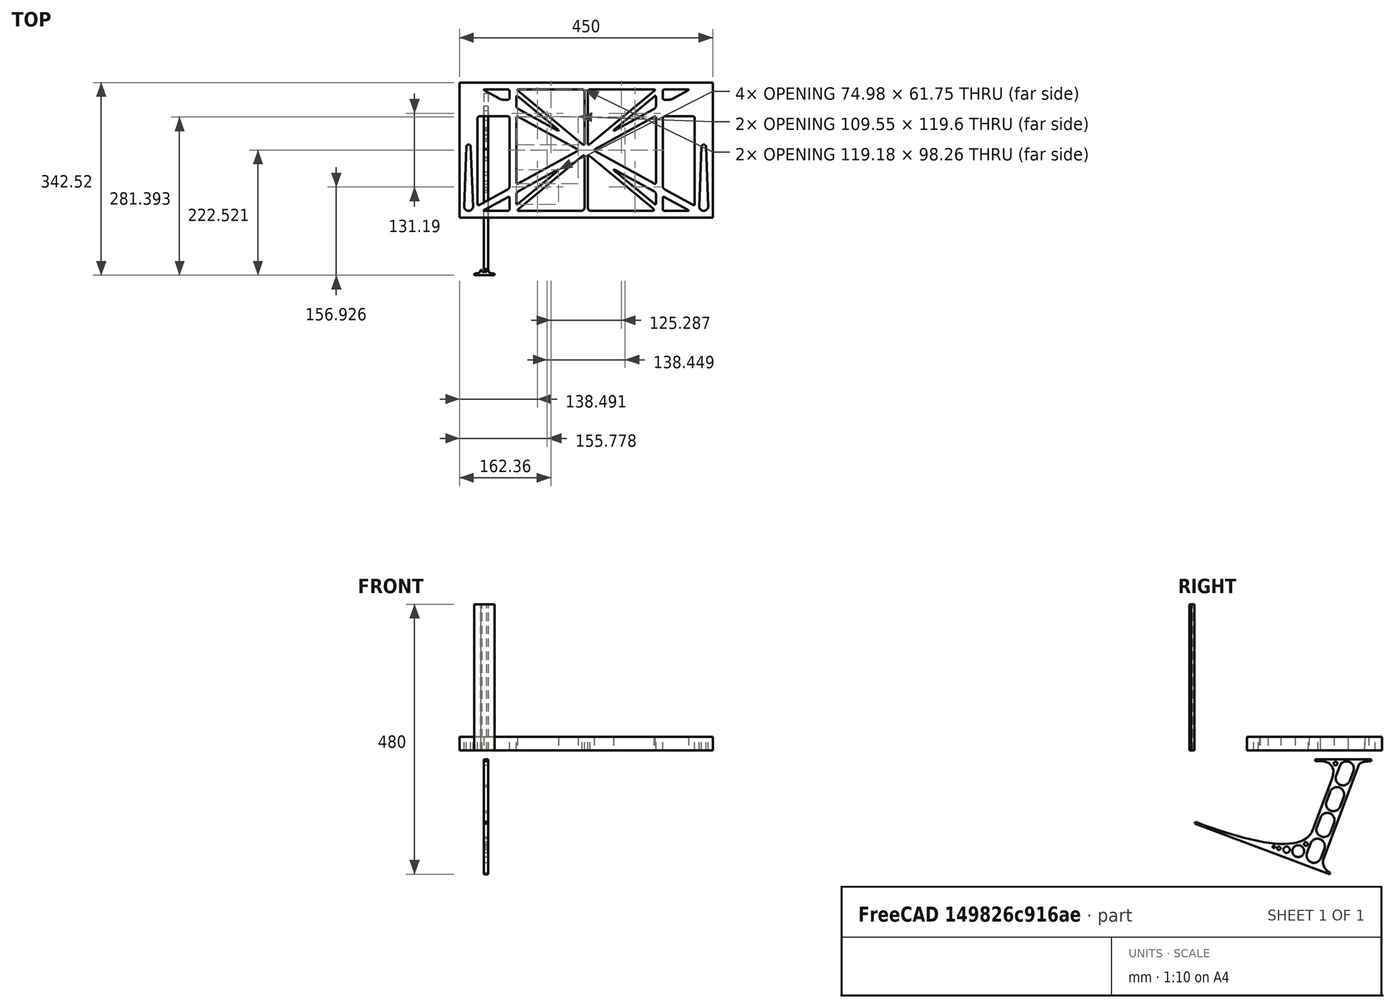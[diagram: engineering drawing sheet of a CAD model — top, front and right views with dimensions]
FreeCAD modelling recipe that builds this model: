
FCSTD DOCUMENT  (FreeCAD 0.19R0.19.2)
Label: laptopStand165FCStd
License: All rights reserved
LicenseURL: http://en.wikipedia.org/wiki/All_rights_reserved
objects: Sketcher::SketchObject×4, Part::Extrusion×3
note: 7 computed .brp shape members not serialized (recipe doc carries the construction recipe); baked Part::Feature solids carry a one-line shape summary decoded from their .brp

FEATURE [Sketcher::SketchObject] Sketch
  FullyConstrained = false
  sketch-geometry (349):
    g0: LineSegment StartX=-10.9272 StartY=-82.7794 StartZ=0 EndX=46.0728 EndY=-51.4823 EndZ=0
    g1: LineSegment StartX=-10.9272 StartY=76.4095 StartZ=0 EndX=-10.9272 EndY=-82.7794 EndZ=0
    g2: LineSegment StartX=46.0728 StartY=76.4095 StartZ=0 EndX=46.0728 EndY=-51.4823 EndZ=0
    g3: LineSegment StartX=-42.9272 StartY=136.221 StartZ=0 EndX=-42.9272 EndY=-103.779 EndZ=0
    g4: LineSegment StartX=407.073 StartY=136.221 StartZ=0 EndX=407.073 EndY=-103.779 EndZ=0
    g5: ArcOfCircle CenterX=-26.9272 CenterY=-83.7794 CenterZ=0 NormalX=0 NormalY=0 NormalZ=1 AngleXU=0 Radius=8 StartAngle=3.14159 EndAngle=6.28319
    g6: ArcOfCircle CenterX=391.073 CenterY=22.1087 CenterZ=0 NormalX=0 NormalY=0 NormalZ=1 AngleXU=0 Radius=8 StartAngle=-4.4e-15 EndAngle=3.14159
    g7: LineSegment StartX=399.073 StartY=22.1087 StartZ=0 EndX=399.073 EndY=-83.7794 EndZ=0
    g8: LineSegment StartX=383.073 StartY=22.1087 StartZ=0 EndX=383.073 EndY=-83.7794 EndZ=0
    g9: ArcOfCircle CenterX=391.073 CenterY=-83.7794 CenterZ=0 NormalX=0 NormalY=0 NormalZ=1 AngleXU=0 Radius=8 StartAngle=3.14159 EndAngle=6.28319
    g10: Circle CenterX=175.022 CenterY=27.0628 CenterZ=0 NormalX=0 NormalY=0 NormalZ=1 AngleXU=0 Radius=1
    g11: Circle CenterX=179.022 CenterY=24.8665 CenterZ=0 NormalX=0 NormalY=0 NormalZ=1 AngleXU=0 Radius=1
    g12: Circle CenterX=179.022 CenterY=27.0628 CenterZ=0 NormalX=0 NormalY=0 NormalZ=1 AngleXU=0 Radius=1
    g13: BSplineCurve PolesCount=3 KnotsCount=2 Degree=2 IsPeriodic=0
    g14: GeomPoint X=175.022 Y=27.0628 Z=0
    g15: GeomPoint X=179.022 Y=27.0628 Z=0
    g16: Circle CenterX=189.124 CenterY=27.0628 CenterZ=0 NormalX=0 NormalY=0 NormalZ=1 AngleXU=0 Radius=1
    g17: Circle CenterX=185.124 CenterY=24.8665 CenterZ=0 NormalX=0 NormalY=0 NormalZ=1 AngleXU=0 Radius=1
    g18: Circle CenterX=185.124 CenterY=27.0628 CenterZ=0 NormalX=0 NormalY=0 NormalZ=1 AngleXU=0 Radius=1
    g19: BSplineCurve PolesCount=3 KnotsCount=2 Degree=2 IsPeriodic=0
    g20: GeomPoint X=189.124 Y=27.0628 Z=0
    g21: GeomPoint X=185.124 Y=27.0628 Z=0
    g22: Circle CenterX=175.022 CenterY=5.37834 CenterZ=0 NormalX=0 NormalY=0 NormalZ=1 AngleXU=0 Radius=1
    g23: Circle CenterX=179.022 CenterY=7.57463 CenterZ=0 NormalX=0 NormalY=0 NormalZ=1 AngleXU=0 Radius=1
    g24: Circle CenterX=179.022 CenterY=5.34704 CenterZ=0 NormalX=0 NormalY=0 NormalZ=1 AngleXU=0 Radius=1
    g25: BSplineCurve PolesCount=3 KnotsCount=2 Degree=2 IsPeriodic=0
    g26: GeomPoint X=175.022 Y=5.37834 Z=0
    g27: GeomPoint X=179.022 Y=5.34704 Z=0
    g28: Circle CenterX=189.124 CenterY=5.37834 CenterZ=0 NormalX=0 NormalY=0 NormalZ=1 AngleXU=0 Radius=1
    g29: Circle CenterX=185.124 CenterY=7.57463 CenterZ=0 NormalX=0 NormalY=0 NormalZ=1 AngleXU=0 Radius=1
    g30: Circle CenterX=185.124 CenterY=5.34704 CenterZ=0 NormalX=0 NormalY=0 NormalZ=1 AngleXU=0 Radius=1
    g31: BSplineCurve PolesCount=3 KnotsCount=2 Degree=2 IsPeriodic=0
    g32: GeomPoint X=189.124 Y=5.37834 Z=0
    g33: GeomPoint X=185.124 Y=5.34704 Z=0
    g34: Circle CenterX=165.871 CenterY=18.1458 CenterZ=0 NormalX=0 NormalY=0 NormalZ=1 AngleXU=0 Radius=1
    g35: Circle CenterX=169.377 CenterY=16.2206 CenterZ=0 NormalX=0 NormalY=0 NormalZ=1 AngleXU=0 Radius=1
    g36: Circle CenterX=165.871 CenterY=14.2954 CenterZ=0 NormalX=0 NormalY=0 NormalZ=1 AngleXU=0 Radius=1
    g37: BSplineCurve PolesCount=3 KnotsCount=2 Degree=2 IsPeriodic=0
    g38: GeomPoint X=165.871 Y=18.1458 Z=0
    g39: GeomPoint X=165.871 Y=14.2954 Z=0
    g40: Circle CenterX=198.275 CenterY=18.1458 CenterZ=0 NormalX=0 NormalY=0 NormalZ=1 AngleXU=0 Radius=1
    g41: Circle CenterX=194.768 CenterY=16.2206 CenterZ=0 NormalX=0 NormalY=0 NormalZ=1 AngleXU=0 Radius=1
    g42: Circle CenterX=198.275 CenterY=14.2954 CenterZ=0 NormalX=0 NormalY=0 NormalZ=1 AngleXU=0 Radius=1
    g43: BSplineCurve PolesCount=3 KnotsCount=2 Degree=2 IsPeriodic=0
    g44: GeomPoint X=198.275 Y=18.1458 Z=0
    g45: GeomPoint X=198.275 Y=14.2954 Z=0
    g46: LineSegment StartX=407.073 StartY=-103.779 StartZ=0 EndX=-42.9272 EndY=-103.779 EndZ=0
    g47: LineSegment StartX=407.073 StartY=136.221 StartZ=0 EndX=-42.9272 EndY=136.221 EndZ=0
    g48: LineSegment StartX=46.0728 StartY=76.4095 StartZ=0 EndX=-10.9272 EndY=76.4095 EndZ=0
    g49: Circle CenterX=125.607 CenterY=54.1951 CenterZ=0 NormalX=0 NormalY=0 NormalZ=1 AngleXU=0 Radius=1
    g50: Circle CenterX=139.632 CenterY=46.4944 CenterZ=0 NormalX=0 NormalY=0 NormalZ=1 AngleXU=0 Radius=1
    g51: Circle CenterX=127.326 CenterY=56.7187 CenterZ=0 NormalX=0 NormalY=0 NormalZ=1 AngleXU=0 Radius=1
    g52: BSplineCurve PolesCount=3 KnotsCount=2 Degree=2 IsPeriodic=0
    g53: GeomPoint X=125.607 Y=54.1951 Z=0
    g54: GeomPoint X=127.326 Y=56.7187 Z=0
    g55: Circle CenterX=236.821 CenterY=56.7187 CenterZ=0 NormalX=0 NormalY=0 NormalZ=1 AngleXU=0 Radius=1
    g56: Circle CenterX=224.513 CenterY=46.4944 CenterZ=0 NormalX=0 NormalY=0 NormalZ=1 AngleXU=0 Radius=1
    g57: Circle CenterX=238.538 CenterY=54.1951 CenterZ=0 NormalX=0 NormalY=0 NormalZ=1 AngleXU=0 Radius=1
    g58: BSplineCurve PolesCount=3 KnotsCount=2 Degree=2 IsPeriodic=0
    g59: GeomPoint X=236.821 Y=56.7187 Z=0
    g60: GeomPoint X=238.538 Y=54.1951 Z=0
    g61: Circle CenterX=238.538 CenterY=-21.7539 CenterZ=0 NormalX=0 NormalY=0 NormalZ=1 AngleXU=0 Radius=1
    g62: Circle CenterX=224.513 CenterY=-14.0532 CenterZ=0 NormalX=0 NormalY=0 NormalZ=1 AngleXU=0 Radius=1
    g63: Circle CenterX=236.821 CenterY=-24.2775 CenterZ=0 NormalX=0 NormalY=0 NormalZ=1 AngleXU=0 Radius=1
    g64: BSplineCurve PolesCount=3 KnotsCount=2 Degree=2 IsPeriodic=0
    g65: GeomPoint X=238.538 Y=-21.7539 Z=0
    g66: GeomPoint X=236.821 Y=-24.2775 Z=0
    g67: Circle CenterX=125.607 CenterY=-21.7539 CenterZ=0 NormalX=0 NormalY=0 NormalZ=1 AngleXU=0 Radius=1
    g68: Circle CenterX=139.632 CenterY=-14.0532 CenterZ=0 NormalX=0 NormalY=0 NormalZ=1 AngleXU=0 Radius=1
    g69: Circle CenterX=127.325 CenterY=-24.2775 CenterZ=0 NormalX=0 NormalY=0 NormalZ=1 AngleXU=0 Radius=1
    g70: BSplineCurve PolesCount=3 KnotsCount=2 Degree=2 IsPeriodic=0
    g71: GeomPoint X=125.607 Y=-21.7539 Z=0
    g72: GeomPoint X=127.325 Y=-24.2775 Z=0
    g73: Circle CenterX=302.996 CenterY=111.695 CenterZ=0 NormalX=0 NormalY=0 NormalZ=1 AngleXU=0 Radius=1
    g74: Circle CenterX=306.073 CenterY=114.251 CenterZ=0 NormalX=0 NormalY=0 NormalZ=1 AngleXU=0 Radius=1
    g75: Circle CenterX=306.073 CenterY=110.251 CenterZ=0 NormalX=0 NormalY=0 NormalZ=1 AngleXU=0 Radius=1
    g76: BSplineCurve PolesCount=3 KnotsCount=2 Degree=2 IsPeriodic=0
    g77: GeomPoint X=302.996 Y=111.695 Z=0
    g78: GeomPoint X=306.073 Y=110.251 Z=0
    g79: Circle CenterX=306.073 CenterY=95.2763 CenterZ=0 NormalX=0 NormalY=0 NormalZ=1 AngleXU=0 Radius=1
    g80: Circle CenterX=306.073 CenterY=91.2763 CenterZ=0 NormalX=0 NormalY=0 NormalZ=1 AngleXU=0 Radius=1
    g81: Circle CenterX=302.567 CenterY=89.3511 CenterZ=0 NormalX=0 NormalY=0 NormalZ=1 AngleXU=0 Radius=1
    g82: BSplineCurve PolesCount=3 KnotsCount=2 Degree=2 IsPeriodic=0
    g83: GeomPoint X=306.073 Y=95.2763 Z=0
    g84: GeomPoint X=302.567 Y=89.3511 Z=0
    g85: LineSegment StartX=306.073 StartY=110.251 StartZ=0 EndX=306.073 EndY=95.2763 EndZ=0
    g86: LineSegment StartX=302.996 StartY=111.695 StartZ=0 EndX=236.821 EndY=56.7187 EndZ=0
    g87: LineSegment StartX=238.538 StartY=54.1951 StartZ=0 EndX=302.567 EndY=89.3511 EndZ=0
    g88: Circle CenterX=61.1496 CenterY=111.695 CenterZ=0 NormalX=0 NormalY=0 NormalZ=1 AngleXU=0 Radius=1
    g89: Circle CenterX=58.0728 CenterY=114.251 CenterZ=0 NormalX=0 NormalY=0 NormalZ=1 AngleXU=0 Radius=1
    g90: Circle CenterX=58.0728 CenterY=110.251 CenterZ=0 NormalX=0 NormalY=0 NormalZ=1 AngleXU=0 Radius=1
    g91: BSplineCurve PolesCount=3 KnotsCount=2 Degree=2 IsPeriodic=0
    g92: GeomPoint X=61.1496 Y=111.695 Z=0
    g93: GeomPoint X=58.0728 Y=110.251 Z=0
    g94: Circle CenterX=61.5791 CenterY=89.3511 CenterZ=0 NormalX=0 NormalY=0 NormalZ=1 AngleXU=0 Radius=1
    g95: Circle CenterX=58.0728 CenterY=91.2763 CenterZ=0 NormalX=0 NormalY=0 NormalZ=1 AngleXU=0 Radius=1
    g96: Circle CenterX=58.0728 CenterY=95.2763 CenterZ=0 NormalX=0 NormalY=0 NormalZ=1 AngleXU=0 Radius=1
    g97: BSplineCurve PolesCount=3 KnotsCount=2 Degree=2 IsPeriodic=0
    g98: GeomPoint X=61.5791 Y=89.3511 Z=0
    g99: GeomPoint X=58.0728 Y=95.2763 Z=0
    g100: LineSegment StartX=58.0728 StartY=110.251 StartZ=0 EndX=58.0728 EndY=95.2763 EndZ=0
    g101: LineSegment StartX=61.1496 StartY=111.695 StartZ=0 EndX=127.326 EndY=56.7187 EndZ=0
    g102: LineSegment StartX=125.607 StartY=54.1951 StartZ=0 EndX=61.5791 EndY=89.3511 EndZ=0
    g103: Circle CenterX=61.5791 CenterY=-56.9099 CenterZ=0 NormalX=0 NormalY=0 NormalZ=1 AngleXU=0 Radius=1
    g104: Circle CenterX=58.0728 CenterY=-58.8351 CenterZ=0 NormalX=0 NormalY=0 NormalZ=1 AngleXU=0 Radius=1
    g105: Circle CenterX=58.0728 CenterY=-62.8351 CenterZ=0 NormalX=0 NormalY=0 NormalZ=1 AngleXU=0 Radius=1
    g106: BSplineCurve PolesCount=3 KnotsCount=2 Degree=2 IsPeriodic=0
    g107: GeomPoint X=61.5791 Y=-56.9099 Z=0
    g108: GeomPoint X=58.0728 Y=-62.8351 Z=0
    g109: Circle CenterX=58.0728 CenterY=-77.8102 CenterZ=0 NormalX=0 NormalY=0 NormalZ=1 AngleXU=0 Radius=1
    g110: Circle CenterX=58.0728 CenterY=-81.8102 CenterZ=0 NormalX=0 NormalY=0 NormalZ=1 AngleXU=0 Radius=1
    g111: Circle CenterX=61.1496 CenterY=-79.2541 CenterZ=0 NormalX=0 NormalY=0 NormalZ=1 AngleXU=0 Radius=1
    g112: BSplineCurve PolesCount=3 KnotsCount=2 Degree=2 IsPeriodic=0
    g113: GeomPoint X=58.0728 Y=-77.8102 Z=0
    g114: GeomPoint X=61.1496 Y=-79.2541 Z=0
    g115: LineSegment StartX=58.0728 StartY=-62.8351 StartZ=0 EndX=58.0728 EndY=-77.8102 EndZ=0
    g116: LineSegment StartX=61.1496 StartY=-79.2541 StartZ=0 EndX=127.325 EndY=-24.2775 EndZ=0
    g117: LineSegment StartX=125.607 StartY=-21.7539 StartZ=0 EndX=61.5791 EndY=-56.9099 EndZ=0
    g118: Circle CenterX=302.567 CenterY=-56.9099 CenterZ=0 NormalX=0 NormalY=0 NormalZ=1 AngleXU=0 Radius=1
    g119: Circle CenterX=306.073 CenterY=-58.8351 CenterZ=0 NormalX=0 NormalY=0 NormalZ=1 AngleXU=0 Radius=1
    g120: Circle CenterX=306.073 CenterY=-62.8351 CenterZ=0 NormalX=0 NormalY=0 NormalZ=1 AngleXU=0 Radius=1
    g121: BSplineCurve PolesCount=3 KnotsCount=2 Degree=2 IsPeriodic=0
    g122: GeomPoint X=302.567 Y=-56.9099 Z=0
    g123: GeomPoint X=306.073 Y=-62.8351 Z=0
    g124: Circle CenterX=302.996 CenterY=-79.2541 CenterZ=0 NormalX=0 NormalY=0 NormalZ=1 AngleXU=0 Radius=1
    g125: Circle CenterX=306.073 CenterY=-81.8102 CenterZ=0 NormalX=0 NormalY=0 NormalZ=1 AngleXU=0 Radius=1
    g126: Circle CenterX=306.073 CenterY=-77.8102 CenterZ=0 NormalX=0 NormalY=0 NormalZ=1 AngleXU=0 Radius=1
    g127: BSplineCurve PolesCount=3 KnotsCount=2 Degree=2 IsPeriodic=0
    g128: GeomPoint X=302.996 Y=-79.2541 Z=0
    g129: GeomPoint X=306.073 Y=-77.8102 Z=0
    g130: LineSegment StartX=306.073 StartY=-62.8351 StartZ=0 EndX=306.073 EndY=-77.8102 EndZ=0
    g131: LineSegment StartX=302.996 StartY=-79.2541 StartZ=0 EndX=236.821 EndY=-24.2775 EndZ=0
    g132: LineSegment StartX=238.538 StartY=-21.7539 StartZ=0 EndX=302.567 EndY=-56.9099 EndZ=0
    g133: Circle CenterX=61.6457 CenterY=-88.8112 CenterZ=0 NormalX=0 NormalY=0 NormalZ=1 AngleXU=0 Radius=1
    g134: Circle CenterX=58.0728 CenterY=-91.7794 CenterZ=0 NormalX=0 NormalY=0 NormalZ=1 AngleXU=0 Radius=1
    g135: Circle CenterX=63.9135 CenterY=-91.7794 CenterZ=0 NormalX=0 NormalY=0 NormalZ=1 AngleXU=0 Radius=1
    g136: BSplineCurve PolesCount=3 KnotsCount=2 Degree=2 IsPeriodic=0
    g137: GeomPoint X=61.6457 Y=-88.8112 Z=0
    g138: GeomPoint X=63.9135 Y=-91.7794 Z=0
    g139: Circle CenterX=179.022 CenterY=-85.8163 CenterZ=0 NormalX=0 NormalY=0 NormalZ=1 AngleXU=0 Radius=1
    g140: Circle CenterX=179.022 CenterY=-91.7794 CenterZ=0 NormalX=0 NormalY=0 NormalZ=1 AngleXU=0 Radius=1
    g141: Circle CenterX=171.895 CenterY=-91.7794 CenterZ=0 NormalX=0 NormalY=0 NormalZ=1 AngleXU=0 Radius=1
    g142: BSplineCurve PolesCount=3 KnotsCount=2 Degree=2 IsPeriodic=0
    g143: GeomPoint X=179.022 Y=-85.8163 Z=0
    g144: GeomPoint X=171.895 Y=-91.7794 Z=0
    g145: Circle CenterX=185.124 CenterY=-86.2028 CenterZ=0 NormalX=0 NormalY=0 NormalZ=1 AngleXU=0 Radius=1
    g146: Circle CenterX=185.124 CenterY=-91.7794 CenterZ=0 NormalX=0 NormalY=0 NormalZ=1 AngleXU=0 Radius=1
    g147: Circle CenterX=191.747 CenterY=-91.7794 CenterZ=0 NormalX=0 NormalY=0 NormalZ=1 AngleXU=0 Radius=1
    g148: BSplineCurve PolesCount=3 KnotsCount=2 Degree=2 IsPeriodic=0
    g149: GeomPoint X=185.124 Y=-86.2028 Z=0
    g150: GeomPoint X=191.747 Y=-91.7794 Z=0
    g151: Circle CenterX=299.888 CenterY=-86.6413 CenterZ=0 NormalX=0 NormalY=0 NormalZ=1 AngleXU=0 Radius=1
    g152: Circle CenterX=306.073 CenterY=-91.7794 CenterZ=0 NormalX=0 NormalY=0 NormalZ=1 AngleXU=0 Radius=1
    g153: Circle CenterX=298.776 CenterY=-91.7794 CenterZ=0 NormalX=0 NormalY=0 NormalZ=1 AngleXU=0 Radius=1
    g154: BSplineCurve PolesCount=3 KnotsCount=2 Degree=2 IsPeriodic=0
    g155: GeomPoint X=299.888 Y=-86.6413 Z=0
    g156: GeomPoint X=298.776 Y=-91.7794 Z=0
    g157: LineSegment StartX=189.124 StartY=5.37834 StartZ=0 EndX=299.888 EndY=-86.6413 EndZ=0
    g158: LineSegment StartX=298.776 StartY=-91.7794 StartZ=0 EndX=191.747 EndY=-91.7794 EndZ=0
    g159: LineSegment StartX=185.124 StartY=-86.2028 StartZ=0 EndX=185.124 EndY=5.34704 EndZ=0
    g160: LineSegment StartX=179.022 StartY=5.34704 StartZ=0 EndX=179.022 EndY=-85.8163 EndZ=0
    g161: LineSegment StartX=171.895 StartY=-91.7794 StartZ=0 EndX=63.9135 EndY=-91.7794 EndZ=0
    g162: LineSegment StartX=61.6457 StartY=-88.8112 StartZ=0 EndX=175.022 EndY=5.37834 EndZ=0
    g163: Circle CenterX=302.073 CenterY=124.221 CenterZ=0 NormalX=0 NormalY=0 NormalZ=1 AngleXU=0 Radius=1
    g164: Circle CenterX=306.073 CenterY=124.221 CenterZ=0 NormalX=0 NormalY=0 NormalZ=1 AngleXU=0 Radius=1
    g165: Circle CenterX=302.996 CenterY=121.665 CenterZ=0 NormalX=0 NormalY=0 NormalZ=1 AngleXU=0 Radius=1
    g166: BSplineCurve PolesCount=3 KnotsCount=2 Degree=2 IsPeriodic=0
    g167: GeomPoint X=302.073 Y=124.221 Z=0
    g168: GeomPoint X=302.996 Y=121.665 Z=0
    g169: Circle CenterX=189.124 CenterY=124.221 CenterZ=0 NormalX=0 NormalY=0 NormalZ=1 AngleXU=0 Radius=1
    g170: Circle CenterX=185.124 CenterY=124.221 CenterZ=0 NormalX=0 NormalY=0 NormalZ=1 AngleXU=0 Radius=1
    g171: Circle CenterX=185.124 CenterY=120.221 CenterZ=0 NormalX=0 NormalY=0 NormalZ=1 AngleXU=0 Radius=1
    g172: BSplineCurve PolesCount=3 KnotsCount=2 Degree=2 IsPeriodic=0
    g173: GeomPoint X=189.124 Y=124.221 Z=0
    g174: GeomPoint X=185.124 Y=120.221 Z=0
    g175: Circle CenterX=175.022 CenterY=124.221 CenterZ=0 NormalX=0 NormalY=0 NormalZ=1 AngleXU=0 Radius=1
    g176: Circle CenterX=179.022 CenterY=124.221 CenterZ=0 NormalX=0 NormalY=0 NormalZ=1 AngleXU=0 Radius=1
    g177: Circle CenterX=179.022 CenterY=120.221 CenterZ=0 NormalX=0 NormalY=0 NormalZ=1 AngleXU=0 Radius=1
    g178: BSplineCurve PolesCount=3 KnotsCount=2 Degree=2 IsPeriodic=0
    g179: GeomPoint X=175.022 Y=124.221 Z=0
    g180: GeomPoint X=179.022 Y=120.221 Z=0
    g181: Circle CenterX=62.0728 CenterY=124.221 CenterZ=0 NormalX=0 NormalY=0 NormalZ=1 AngleXU=0 Radius=1
    g182: Circle CenterX=58.0728 CenterY=124.221 CenterZ=0 NormalX=0 NormalY=0 NormalZ=1 AngleXU=0 Radius=1
    g183: Circle CenterX=61.1496 CenterY=121.665 CenterZ=0 NormalX=0 NormalY=0 NormalZ=1 AngleXU=0 Radius=1
    g184: BSplineCurve PolesCount=3 KnotsCount=2 Degree=2 IsPeriodic=0
    g185: GeomPoint X=62.0728 Y=124.221 Z=0
    g186: GeomPoint X=61.1496 Y=121.665 Z=0
    g187: LineSegment StartX=62.0728 StartY=124.221 StartZ=0 EndX=175.022 EndY=124.221 EndZ=0
    g188: LineSegment StartX=179.022 StartY=120.221 StartZ=0 EndX=179.022 EndY=27.0628 EndZ=0
    g189: LineSegment StartX=185.124 StartY=27.0628 StartZ=0 EndX=185.124 EndY=120.221 EndZ=0
    g190: LineSegment StartX=189.124 StartY=124.221 StartZ=0 EndX=302.073 EndY=124.221 EndZ=0
    g191: LineSegment StartX=302.996 StartY=121.665 StartZ=0 EndX=189.124 EndY=27.0628 EndZ=0
    g192: LineSegment StartX=175.022 StartY=27.0628 StartZ=0 EndX=61.1496 EndY=121.665 EndZ=0
    g193: Circle CenterX=61.5791 CenterY=75.4095 CenterZ=0 NormalX=0 NormalY=0 NormalZ=1 AngleXU=0 Radius=1
    g194: Circle CenterX=58.0728 CenterY=77.3346 CenterZ=0 NormalX=0 NormalY=0 NormalZ=1 AngleXU=0 Radius=1
    g195: Circle CenterX=58.0728 CenterY=73.3346 CenterZ=0 NormalX=0 NormalY=0 NormalZ=1 AngleXU=0 Radius=1
    g196: BSplineCurve PolesCount=3 KnotsCount=2 Degree=2 IsPeriodic=0
    g197: GeomPoint X=61.5791 Y=75.4095 Z=0
    g198: GeomPoint X=58.0728 Y=73.3346 Z=0
    g199: Circle CenterX=58.0728 CenterY=-40.8935 CenterZ=0 NormalX=0 NormalY=0 NormalZ=1 AngleXU=0 Radius=1
    g200: Circle CenterX=58.0728 CenterY=-44.8935 CenterZ=0 NormalX=0 NormalY=0 NormalZ=1 AngleXU=0 Radius=1
    g201: Circle CenterX=61.5791 CenterY=-42.9683 CenterZ=0 NormalX=0 NormalY=0 NormalZ=1 AngleXU=0 Radius=1
    g202: BSplineCurve PolesCount=3 KnotsCount=2 Degree=2 IsPeriodic=0
    g203: GeomPoint X=58.0728 Y=-40.8935 Z=0
    g204: GeomPoint X=61.5791 Y=-42.9683 Z=0
    g205: LineSegment StartX=61.5791 StartY=-42.9683 StartZ=0 EndX=165.871 EndY=14.2954 EndZ=0
    g206: LineSegment StartX=165.871 StartY=18.1458 StartZ=0 EndX=61.5791 EndY=75.4095 EndZ=0
    g207: LineSegment StartX=58.0728 StartY=73.3346 StartZ=0 EndX=58.0728 EndY=-40.8935 EndZ=0
    g208: Circle CenterX=302.567 CenterY=-42.9683 CenterZ=0 NormalX=0 NormalY=0 NormalZ=1 AngleXU=0 Radius=1
    g209: Circle CenterX=306.073 CenterY=-44.8935 CenterZ=0 NormalX=0 NormalY=0 NormalZ=1 AngleXU=0 Radius=1
    g210: Circle CenterX=306.073 CenterY=-40.8935 CenterZ=0 NormalX=0 NormalY=0 NormalZ=1 AngleXU=0 Radius=1
    g211: BSplineCurve PolesCount=3 KnotsCount=2 Degree=2 IsPeriodic=0
    g212: GeomPoint X=302.567 Y=-42.9683 Z=0
    g213: GeomPoint X=306.073 Y=-40.8935 Z=0
    g214: Circle CenterX=306.073 CenterY=73.3346 CenterZ=0 NormalX=0 NormalY=0 NormalZ=1 AngleXU=0 Radius=1
    g215: Circle CenterX=306.073 CenterY=77.3346 CenterZ=0 NormalX=0 NormalY=0 NormalZ=1 AngleXU=0 Radius=1
    g216: Circle CenterX=302.567 CenterY=75.4095 CenterZ=0 NormalX=0 NormalY=0 NormalZ=1 AngleXU=0 Radius=1
    g217: BSplineCurve PolesCount=3 KnotsCount=2 Degree=2 IsPeriodic=0
    g218: GeomPoint X=306.073 Y=73.3346 Z=0
    g219: GeomPoint X=302.567 Y=75.4095 Z=0
    g220: LineSegment StartX=302.567 StartY=-42.9683 StartZ=0 EndX=198.275 EndY=14.2954 EndZ=0
    g221: LineSegment StartX=198.275 StartY=18.1458 StartZ=0 EndX=302.567 EndY=75.4095 EndZ=0
    g222: LineSegment StartX=306.073 StartY=73.3346 StartZ=0 EndX=306.073 EndY=-40.8935 EndZ=0
    g223: LineSegment StartX=322.073 StartY=105.865 StartZ=0 EndX=328.643 EndY=105.865 EndZ=0
    g224: LineSegment StartX=318.073 StartY=120.221 StartZ=0 EndX=318.073 EndY=109.865 EndZ=0
    g225: LineSegment StartX=336.157 StartY=107.779 StartZ=0 EndX=362.567 EndY=122.294 EndZ=0
    g226: Circle CenterX=362.073 CenterY=124.221 CenterZ=0 NormalX=0 NormalY=0 NormalZ=1 AngleXU=0 Radius=1
    g227: Circle CenterX=366.073 CenterY=124.221 CenterZ=0 NormalX=0 NormalY=0 NormalZ=1 AngleXU=0 Radius=1
    g228: Circle CenterX=362.567 CenterY=122.294 CenterZ=0 NormalX=0 NormalY=0 NormalZ=1 AngleXU=0 Radius=1
    g229: BSplineCurve PolesCount=3 KnotsCount=2 Degree=2 IsPeriodic=0
    g230: GeomPoint X=362.073 Y=124.221 Z=0
    g231: GeomPoint X=362.567 Y=122.294 Z=0
    g232: Circle CenterX=322.073 CenterY=124.221 CenterZ=0 NormalX=0 NormalY=0 NormalZ=1 AngleXU=0 Radius=1
    g233: Circle CenterX=318.073 CenterY=124.221 CenterZ=0 NormalX=0 NormalY=0 NormalZ=1 AngleXU=0 Radius=1
    g234: Circle CenterX=318.073 CenterY=120.221 CenterZ=0 NormalX=0 NormalY=0 NormalZ=1 AngleXU=0 Radius=1
    g235: BSplineCurve PolesCount=3 KnotsCount=2 Degree=2 IsPeriodic=0
    g236: GeomPoint X=322.073 Y=124.221 Z=0
    g237: GeomPoint X=318.073 Y=120.221 Z=0
    g238: Circle CenterX=322.073 CenterY=105.865 CenterZ=0 NormalX=0 NormalY=0 NormalZ=1 AngleXU=0 Radius=1
    g239: Circle CenterX=318.073 CenterY=105.865 CenterZ=0 NormalX=0 NormalY=0 NormalZ=1 AngleXU=0 Radius=1
    g240: Circle CenterX=318.073 CenterY=109.865 CenterZ=0 NormalX=0 NormalY=0 NormalZ=1 AngleXU=0 Radius=1
    g241: BSplineCurve PolesCount=3 KnotsCount=2 Degree=2 IsPeriodic=0
    g242: GeomPoint X=322.073 Y=105.865 Z=0
    g243: GeomPoint X=318.073 Y=109.865 Z=0
    g244: Circle CenterX=336.157 CenterY=107.779 CenterZ=0 NormalX=0 NormalY=0 NormalZ=1 AngleXU=0 Radius=1
    g245: Circle CenterX=332.651 CenterY=105.853 CenterZ=0 NormalX=0 NormalY=0 NormalZ=1 AngleXU=0 Radius=1
    g246: Circle CenterX=328.643 CenterY=105.865 CenterZ=0 NormalX=0 NormalY=0 NormalZ=1 AngleXU=0 Radius=1
    g247: BSplineCurve PolesCount=3 KnotsCount=2 Degree=2 IsPeriodic=0
    g248: GeomPoint X=336.157 Y=107.779 Z=0
    g249: GeomPoint X=328.643 Y=105.865 Z=0
    g250: LineSegment StartX=322.073 StartY=124.221 StartZ=0 EndX=362.073 EndY=124.221 EndZ=0
    g251: Circle CenterX=371.567 CenterY=-80.8644 CenterZ=0 NormalX=0 NormalY=0 NormalZ=1 AngleXU=0 Radius=1
    g252: Circle CenterX=375.073 CenterY=-82.7896 CenterZ=0 NormalX=0 NormalY=0 NormalZ=1 AngleXU=0 Radius=1
    g253: Circle CenterX=375.073 CenterY=-78.7896 CenterZ=0 NormalX=0 NormalY=0 NormalZ=1 AngleXU=0 Radius=1
    g254: BSplineCurve PolesCount=3 KnotsCount=2 Degree=2 IsPeriodic=0
    g255: GeomPoint X=371.567 Y=-80.8644 Z=0
    g256: GeomPoint X=375.073 Y=-78.7896 Z=0
    g257: Circle CenterX=321.579 CenterY=-53.4075 CenterZ=0 NormalX=0 NormalY=0 NormalZ=1 AngleXU=0 Radius=1
    g258: Circle CenterX=318.073 CenterY=-51.4823 CenterZ=0 NormalX=0 NormalY=0 NormalZ=1 AngleXU=0 Radius=1
    g259: Circle CenterX=318.073 CenterY=-47.4805 CenterZ=0 NormalX=0 NormalY=0 NormalZ=1 AngleXU=0 Radius=1
    g260: BSplineCurve PolesCount=3 KnotsCount=2 Degree=2 IsPeriodic=0
    g261: GeomPoint X=321.579 Y=-53.4075 Z=0
    g262: GeomPoint X=318.073 Y=-47.4805 Z=0
    g263: LineSegment StartX=371.567 StartY=-80.8644 StartZ=0 EndX=321.579 EndY=-53.4075 EndZ=0
    g264: Circle CenterX=321.579 CenterY=-67.3492 CenterZ=0 NormalX=0 NormalY=0 NormalZ=1 AngleXU=0 Radius=1
    g265: Circle CenterX=318.073 CenterY=-65.424 CenterZ=0 NormalX=0 NormalY=0 NormalZ=1 AngleXU=0 Radius=1
    g266: Circle CenterX=318.073 CenterY=-69.424 CenterZ=0 NormalX=0 NormalY=0 NormalZ=1 AngleXU=0 Radius=1
    g267: BSplineCurve PolesCount=3 KnotsCount=2 Degree=2 IsPeriodic=0
    g268: GeomPoint X=321.579 Y=-67.3492 Z=0
    g269: GeomPoint X=318.073 Y=-69.424 Z=0
    g270: Circle CenterX=362.567 CenterY=-89.8542 CenterZ=0 NormalX=0 NormalY=0 NormalZ=1 AngleXU=0 Radius=1
    g271: Circle CenterX=366.073 CenterY=-91.7794 CenterZ=0 NormalX=0 NormalY=0 NormalZ=1 AngleXU=0 Radius=1
    g272: Circle CenterX=362.073 CenterY=-91.7794 CenterZ=0 NormalX=0 NormalY=0 NormalZ=1 AngleXU=0 Radius=1
    g273: BSplineCurve PolesCount=3 KnotsCount=2 Degree=2 IsPeriodic=0
    g274: GeomPoint X=362.567 Y=-89.8542 Z=0
    g275: GeomPoint X=362.073 Y=-91.7794 Z=0
    g276: Circle CenterX=322.073 CenterY=-91.7794 CenterZ=0 NormalX=0 NormalY=0 NormalZ=1 AngleXU=0 Radius=1
    g277: Circle CenterX=318.073 CenterY=-91.7794 CenterZ=0 NormalX=0 NormalY=0 NormalZ=1 AngleXU=0 Radius=1
    g278: Circle CenterX=318.073 CenterY=-87.7794 CenterZ=0 NormalX=0 NormalY=0 NormalZ=1 AngleXU=0 Radius=1
    g279: BSplineCurve PolesCount=3 KnotsCount=2 Degree=2 IsPeriodic=0
    g280: GeomPoint X=322.073 Y=-91.7794 Z=0
    g281: GeomPoint X=318.073 Y=-87.7794 Z=0
    g282: LineSegment StartX=362.567 StartY=-89.8542 StartZ=0 EndX=321.579 EndY=-67.3492 EndZ=0
    g283: LineSegment StartX=318.073 StartY=-69.424 StartZ=0 EndX=318.073 EndY=-87.7794 EndZ=0
    g284: LineSegment StartX=322.073 StartY=-91.7794 StartZ=0 EndX=362.073 EndY=-91.7794 EndZ=0
    g285: Circle CenterX=2.07281 CenterY=124.221 CenterZ=0 NormalX=0 NormalY=0 NormalZ=1 AngleXU=0 Radius=1
    g286: Circle CenterX=1.57905 CenterY=122.295 CenterZ=0 NormalX=0 NormalY=0 NormalZ=1 AngleXU=0 Radius=1
    g287: BSplineCurve PolesCount=3 KnotsCount=2 Degree=2 IsPeriodic=0
    g288: GeomPoint X=2.07281 Y=124.221 Z=0
    g289: GeomPoint X=1.57905 Y=122.295 Z=0
    g290: Circle CenterX=42.0728 CenterY=124.221 CenterZ=0 NormalX=0 NormalY=0 NormalZ=1 AngleXU=0 Radius=1
    g291: Circle CenterX=46.0728 CenterY=124.221 CenterZ=0 NormalX=0 NormalY=0 NormalZ=1 AngleXU=0 Radius=1
    g292: Circle CenterX=46.0728 CenterY=120.221 CenterZ=0 NormalX=0 NormalY=0 NormalZ=1 AngleXU=0 Radius=1
    g293: BSplineCurve PolesCount=3 KnotsCount=2 Degree=2 IsPeriodic=0
    g294: GeomPoint X=42.0728 Y=124.221 Z=0
    g295: GeomPoint X=46.0728 Y=120.221 Z=0
    g296: Circle CenterX=46.0728 CenterY=109.865 CenterZ=0 NormalX=0 NormalY=0 NormalZ=1 AngleXU=0 Radius=1
    g297: Circle CenterX=46.0728 CenterY=105.865 CenterZ=0 NormalX=0 NormalY=0 NormalZ=1 AngleXU=0 Radius=1
    g298: Circle CenterX=42.0728 CenterY=105.865 CenterZ=0 NormalX=0 NormalY=0 NormalZ=1 AngleXU=0 Radius=1
    g299: BSplineCurve PolesCount=3 KnotsCount=2 Degree=2 IsPeriodic=0
    g300: GeomPoint X=46.0728 Y=109.865 Z=0
    g301: GeomPoint X=42.0728 Y=105.865 Z=0
    g302: Circle CenterX=35.5028 CenterY=105.865 CenterZ=0 NormalX=0 NormalY=0 NormalZ=1 AngleXU=0 Radius=1
    g303: Circle CenterX=31.5028 CenterY=105.865 CenterZ=0 NormalX=0 NormalY=0 NormalZ=1 AngleXU=0 Radius=1
    g304: Circle CenterX=27.9965 CenterY=107.79 CenterZ=0 NormalX=0 NormalY=0 NormalZ=1 AngleXU=0 Radius=1
    g305: BSplineCurve PolesCount=3 KnotsCount=2 Degree=2 IsPeriodic=0
    g306: GeomPoint X=35.5028 Y=105.865 Z=0
    g307: GeomPoint X=27.9965 Y=107.79 Z=0
    g308: LineSegment StartX=2.07281 StartY=124.221 StartZ=0 EndX=42.0728 EndY=124.221 EndZ=0
    g309: LineSegment StartX=46.0728 StartY=120.221 StartZ=0 EndX=46.0728 EndY=109.865 EndZ=0
    g310: LineSegment StartX=42.0728 StartY=105.865 StartZ=0 EndX=35.5028 EndY=105.865 EndZ=0
    g311: LineSegment StartX=27.9965 StartY=107.79 StartZ=0 EndX=1.57905 EndY=122.295 EndZ=0
    g312: Circle CenterX=42.5666 CenterY=-67.3492 CenterZ=0 NormalX=0 NormalY=0 NormalZ=1 AngleXU=0 Radius=1
    g313: Circle CenterX=46.0728 CenterY=-65.424 CenterZ=0 NormalX=0 NormalY=0 NormalZ=1 AngleXU=0 Radius=1
    g314: Circle CenterX=46.0728 CenterY=-69.424 CenterZ=0 NormalX=0 NormalY=0 NormalZ=1 AngleXU=0 Radius=1
    g315: BSplineCurve PolesCount=3 KnotsCount=2 Degree=2 IsPeriodic=0
    g316: GeomPoint X=42.5666 Y=-67.3492 Z=0
    g317: GeomPoint X=46.0728 Y=-69.424 Z=0
    g318: Circle CenterX=46.0728 CenterY=-87.7794 CenterZ=0 NormalX=0 NormalY=0 NormalZ=1 AngleXU=0 Radius=1
    g319: Circle CenterX=46.0728 CenterY=-91.7794 CenterZ=0 NormalX=0 NormalY=0 NormalZ=1 AngleXU=0 Radius=1
    g320: Circle CenterX=42.0728 CenterY=-91.7794 CenterZ=0 NormalX=0 NormalY=0 NormalZ=1 AngleXU=0 Radius=1
    g321: BSplineCurve PolesCount=3 KnotsCount=2 Degree=2 IsPeriodic=0
    g322: GeomPoint X=46.0728 Y=-87.7794 Z=0
    g323: GeomPoint X=42.0728 Y=-91.7794 Z=0
    g324: Circle CenterX=2.07281 CenterY=-91.7794 CenterZ=0 NormalX=0 NormalY=0 NormalZ=1 AngleXU=0 Radius=1
    g325: Circle CenterX=-1.92719 CenterY=-91.7794 CenterZ=0 NormalX=0 NormalY=0 NormalZ=1 AngleXU=0 Radius=1
    g326: Circle CenterX=1.57905 CenterY=-89.8542 CenterZ=0 NormalX=0 NormalY=0 NormalZ=1 AngleXU=0 Radius=1
    g327: BSplineCurve PolesCount=3 KnotsCount=2 Degree=2 IsPeriodic=0
    g328: GeomPoint X=2.07281 Y=-91.7794 Z=0
    g329: GeomPoint X=1.57905 Y=-89.8542 Z=0
    g330: LineSegment StartX=2.07281 StartY=-91.7794 StartZ=0 EndX=42.0728 EndY=-91.7794 EndZ=0
    g331: LineSegment StartX=46.0728 StartY=-87.7794 StartZ=0 EndX=46.0728 EndY=-69.424 EndZ=0
    g332: LineSegment StartX=42.5666 StartY=-67.3492 StartZ=0 EndX=1.57905 EndY=-89.8542 EndZ=0
    g333: Circle CenterX=322.073 CenterY=76.4095 CenterZ=0 NormalX=0 NormalY=0 NormalZ=1 AngleXU=0 Radius=4
    g334: BSplineCurve PolesCount=3 KnotsCount=2 Degree=2 IsPeriodic=0
    g335: GeomPoint X=318.073 Y=72.4095 Z=0
    g336: GeomPoint X=322.073 Y=76.4095 Z=0
    g337: Circle CenterX=375.073 CenterY=72.4095 CenterZ=0 NormalX=0 NormalY=0 NormalZ=1 AngleXU=0 Radius=1
    g338: Circle CenterX=375.073 CenterY=76.4095 CenterZ=0 NormalX=0 NormalY=0 NormalZ=1 AngleXU=0 Radius=1
    g339: Circle CenterX=371.073 CenterY=76.4095 CenterZ=0 NormalX=0 NormalY=0 NormalZ=1 AngleXU=0 Radius=1
    g340: BSplineCurve PolesCount=3 KnotsCount=2 Degree=2 IsPeriodic=0
    g341: GeomPoint X=375.073 Y=72.4095 Z=0
    g342: GeomPoint X=371.073 Y=76.4095 Z=0
    g343: LineSegment StartX=322.073 StartY=76.4095 StartZ=0 EndX=371.073 EndY=76.4095 EndZ=0
    g344: LineSegment StartX=318.073 StartY=72.4095 StartZ=0 EndX=318.073 EndY=-47.4805 EndZ=0
    g345: LineSegment StartX=375.073 StartY=72.4095 StartZ=0 EndX=375.073 EndY=-78.7896 EndZ=0
    g346: ArcOfCircle CenterX=-26.9272 CenterY=22.1087 CenterZ=0 NormalX=0 NormalY=0 NormalZ=1 AngleXU=0 Radius=4 StartAngle=5e-16 EndAngle=3.14159
    g347: LineSegment StartX=-30.9272 StartY=22.1087 StartZ=0 EndX=-34.9272 EndY=-83.7794 EndZ=0
    g348: LineSegment StartX=-18.9272 StartY=-83.7794 StartZ=0 EndX=-22.9272 EndY=22.1087 EndZ=0
  constraints (572):
    c: Coincident(g0,g2)
    c: Block(g0)
    c: Block(g1)
    c: Vertical(g3)
    c: Vertical(g4)
    c: Block(g4)
    c: Block(g3)
    c: Tangent(g6,g7) = 1.5708
    c: Tangent(g7,g9) = 1.5708
    c: Equal(g6,g9)
    c: Coincident(g8,g6)
    c: Coincident(g8,g9)
    c: Block(g7)
    c: Block(g8)
    c: Weight(g10) = 1
    c: Equal(g10,g11)
    c: Equal(g10,g12)
    c: InternalAlignment(g10,g13)
    c: InternalAlignment(g11,g13)
    c: InternalAlignment(g12,g13)
    c: InternalAlignment(g14,g13)
    c: InternalAlignment(g15,g13)
    c: Weight(g16) = 1
    c: Equal(g16,g17)
    c: Equal(g16,g18)
    c: InternalAlignment(g16,g19)
    c: InternalAlignment(g17,g19)
    c: InternalAlignment(g18,g19)
    c: InternalAlignment(g20,g19)
    c: InternalAlignment(g21,g19)
    c: Block(g19)
    c: Block(g13)
    c: Weight(g22) = 1
    c: Equal(g22,g23)
    c: Equal(g22,g24)
    c: InternalAlignment(g22,g25)
    c: InternalAlignment(g23,g25)
    c: InternalAlignment(g24,g25)
    c: InternalAlignment(g26,g25)
    c: InternalAlignment(g27,g25)
    c: Weight(g28) = 1
    c: Equal(g28,g29)
    c: Equal(g28,g30)
    c: InternalAlignment(g28,g31)
    c: InternalAlignment(g29,g31)
    c: InternalAlignment(g30,g31)
    c: InternalAlignment(g32,g31)
    c: InternalAlignment(g33,g31)
    c: Block(g31)
    c: Block(g25)
    c: Weight(g34) = 1
    c: Equal(g34,g35)
    c: Equal(g34,g36)
    c: InternalAlignment(g34,g37)
    c: InternalAlignment(g35,g37)
    c: InternalAlignment(g36,g37)
    c: InternalAlignment(g38,g37)
    c: InternalAlignment(g39,g37)
    c: Weight(g40) = 1
    c: Equal(g40,g41)
    c: Equal(g40,g42)
    c: InternalAlignment(g40,g43)
    c: InternalAlignment(g41,g43)
    c: InternalAlignment(g42,g43)
    c: InternalAlignment(g44,g43)
    c: InternalAlignment(g45,g43)
    c: Block(g37)
    c: Block(g43)
    c: Coincident(g46,g4)
    c: Coincident(g46,g3)
    c: Horizontal(g46)
    c: Distance(g46) = 450
    c: Coincident(g47,g4)
    c: Coincident(g47,g3)
    c: Horizontal(g47)
    c: Horizontal(g48)
    c: Coincident(g2,g48)
    c: Block(g48)
    c: Coincident(g1,g48)
    c: Weight(g49) = 1
    c: Equal(g49,g50)
    c: Equal(g49,g51)
    c: InternalAlignment(g49,g52)
    c: InternalAlignment(g50,g52)
    c: InternalAlignment(g51,g52)
    c: InternalAlignment(g53,g52)
    c: InternalAlignment(g54,g52)
    c: Block(g52)
    c: Weight(g55) = 1
    c: Equal(g55,g56)
    c: Equal(g55,g57)
    c: InternalAlignment(g55,g58)
    c: InternalAlignment(g56,g58)
    c: InternalAlignment(g57,g58)
    c: InternalAlignment(g59,g58)
    c: InternalAlignment(g60,g58)
    c: Block(g58)
    c: Weight(g61) = 1
    c: Equal(g61,g62)
    c: Equal(g61,g63)
    c: InternalAlignment(g61,g64)
    c: InternalAlignment(g62,g64)
    c: InternalAlignment(g63,g64)
    c: InternalAlignment(g65,g64)
    c: InternalAlignment(g66,g64)
    c: Block(g64)
    c: Weight(g67) = 1
    c: Equal(g67,g68)
    c: Equal(g67,g69)
    c: InternalAlignment(g67,g70)
    c: InternalAlignment(g68,g70)
    c: InternalAlignment(g69,g70)
    c: InternalAlignment(g71,g70)
    c: InternalAlignment(g72,g70)
    c: Block(g70)
    c: Weight(g73) = 1
    c: Equal(g73,g74)
    c: Equal(g73,g75)
    c: InternalAlignment(g73,g76)
    c: InternalAlignment(g74,g76)
    c: InternalAlignment(g75,g76)
    c: InternalAlignment(g77,g76)
    c: InternalAlignment(g78,g76)
    c: Weight(g79) = 1
    c: Equal(g79,g80)
    c: Equal(g79,g81)
    c: InternalAlignment(g79,g82)
    c: InternalAlignment(g80,g82)
    c: InternalAlignment(g81,g82)
    c: InternalAlignment(g83,g82)
    c: InternalAlignment(g84,g82)
    c: Block(g76)
    c: Block(g82)
    c: Coincident(g85,g76)
    c: Coincident(g85,g82)
    c: Vertical(g85)
    c: Coincident(g86,g76)
    c: Coincident(g86,g58)
    c: Coincident(g87,g58)
    c: Coincident(g87,g82)
    c: Weight(g88) = 1
    c: Equal(g88,g89)
    c: Equal(g88,g90)
    c: InternalAlignment(g88,g91)
    c: InternalAlignment(g89,g91)
    c: InternalAlignment(g90,g91)
    c: InternalAlignment(g92,g91)
    c: InternalAlignment(g93,g91)
    c: Weight(g94) = 1
    c: Equal(g94,g95)
    c: Equal(g94,g96)
    c: InternalAlignment(g94,g97)
    c: InternalAlignment(g95,g97)
    c: InternalAlignment(g96,g97)
    c: InternalAlignment(g98,g97)
    c: InternalAlignment(g99,g97)
    c: Block(g91)
    c: Block(g97)
    c: Coincident(g100,g91)
    c: Coincident(g100,g97)
    c: Vertical(g100)
    c: Coincident(g101,g91)
    c: Coincident(g101,g52)
    c: Coincident(g102,g52)
    c: Coincident(g102,g97)
    c: Weight(g103) = 1
    c: Equal(g103,g104)
    c: Equal(g103,g105)
    c: InternalAlignment(g103,g106)
    c: InternalAlignment(g104,g106)
    c: InternalAlignment(g105,g106)
    c: InternalAlignment(g107,g106)
    c: InternalAlignment(g108,g106)
    c: Weight(g109) = 1
    c: Equal(g109,g110)
    c: Equal(g109,g111)
    c: InternalAlignment(g109,g112)
    c: InternalAlignment(g110,g112)
    c: InternalAlignment(g111,g112)
    c: InternalAlignment(g113,g112)
    c: InternalAlignment(g114,g112)
    c: Block(g106)
    c: Block(g112)
    c: Coincident(g115,g106)
    c: Coincident(g115,g112)
    c: Vertical(g115)
    c: Coincident(g116,g112)
    c: Coincident(g116,g70)
    c: Coincident(g117,g70)
    c: Coincident(g117,g106)
    c: Weight(g118) = 1
    c: Equal(g118,g119)
    c: Equal(g118,g120)
    c: InternalAlignment(g118,g121)
    c: InternalAlignment(g119,g121)
    c: InternalAlignment(g120,g121)
    c: InternalAlignment(g122,g121)
    c: InternalAlignment(g123,g121)
    c: Weight(g124) = 1
    c: Equal(g124,g125)
    c: Equal(g124,g126)
    c: InternalAlignment(g124,g127)
    c: InternalAlignment(g125,g127)
    c: InternalAlignment(g126,g127)
    c: InternalAlignment(g128,g127)
    c: InternalAlignment(g129,g127)
    c: Block(g121)
    c: Block(g127)
    c: Coincident(g130,g121)
    c: Coincident(g130,g127)
    c: Vertical(g130)
    c: Coincident(g131,g127)
    c: Coincident(g131,g64)
    c: Coincident(g132,g64)
    c: Coincident(g132,g121)
    c: Weight(g133) = 1
    c: Equal(g133,g134)
    c: Equal(g133,g135)
    c: InternalAlignment(g133,g136)
    c: InternalAlignment(g134,g136)
    c: InternalAlignment(g135,g136)
    c: InternalAlignment(g137,g136)
    c: InternalAlignment(g138,g136)
    c: Weight(g139) = 1
    c: Equal(g139,g140)
    c: Equal(g139,g141)
    c: InternalAlignment(g139,g142)
    c: InternalAlignment(g140,g142)
    c: InternalAlignment(g141,g142)
    c: InternalAlignment(g143,g142)
    c: InternalAlignment(g144,g142)
    c: Weight(g145) = 1
    c: Equal(g145,g146)
    c: Equal(g145,g147)
    c: InternalAlignment(g145,g148)
    c: InternalAlignment(g146,g148)
    c: InternalAlignment(g147,g148)
    c: InternalAlignment(g149,g148)
    c: InternalAlignment(g150,g148)
    c: Weight(g151) = 1
    c: Equal(g151,g152)
    c: Equal(g151,g153)
    c: InternalAlignment(g151,g154)
    c: InternalAlignment(g152,g154)
    c: InternalAlignment(g153,g154)
    c: InternalAlignment(g155,g154)
    c: InternalAlignment(g156,g154)
    c: Block(g154)
    c: Block(g148)
    c: Block(g142)
    c: Block(g136)
    c: Coincident(g157,g31)
    c: Coincident(g157,g154)
    c: Coincident(g158,g154)
    c: Coincident(g158,g148)
    c: Horizontal(g158)
    c: Coincident(g159,g148)
    c: Coincident(g159,g31)
    c: Vertical(g159)
    c: Coincident(g160,g25)
    c: Coincident(g160,g142)
    c: Vertical(g160)
    c: Coincident(g161,g142)
    c: Coincident(g161,g136)
    c: Horizontal(g161)
    c: Coincident(g162,g136)
    c: Coincident(g162,g25)
    c: Weight(g163) = 1
    c: Equal(g163,g164)
    c: Equal(g163,g165)
    c: InternalAlignment(g163,g166)
    c: InternalAlignment(g164,g166)
    c: InternalAlignment(g165,g166)
    c: InternalAlignment(g167,g166)
    c: InternalAlignment(g168,g166)
    c: Weight(g169) = 1
    c: Equal(g169,g170)
    c: Equal(g169,g171)
    c: InternalAlignment(g169,g172)
    c: InternalAlignment(g170,g172)
    c: InternalAlignment(g171,g172)
    c: InternalAlignment(g173,g172)
    c: InternalAlignment(g174,g172)
    c: Weight(g175) = 1
    c: Equal(g175,g176)
    c: Equal(g175,g177)
    c: InternalAlignment(g175,g178)
    c: InternalAlignment(g176,g178)
    c: InternalAlignment(g177,g178)
    c: InternalAlignment(g179,g178)
    c: InternalAlignment(g180,g178)
    c: Weight(g181) = 1
    c: Equal(g181,g182)
    c: Equal(g181,g183)
    c: InternalAlignment(g181,g184)
    c: InternalAlignment(g182,g184)
    c: InternalAlignment(g183,g184)
    c: InternalAlignment(g185,g184)
    c: InternalAlignment(g186,g184)
    c: Block(g184)
    c: Block(g178)
    c: Block(g172)
    c: Block(g166)
    c: Coincident(g187,g184)
    c: Coincident(g187,g178)
    c: Horizontal(g187)
    c: Coincident(g188,g178)
    c: Coincident(g188,g13)
    c: Vertical(g188)
    c: Coincident(g189,g19)
    c: Coincident(g189,g172)
    c: Vertical(g189)
    c: Coincident(g190,g172)
    c: Coincident(g190,g166)
    c: Horizontal(g190)
    c: Coincident(g191,g166)
    c: Coincident(g191,g19)
    c: Coincident(g192,g13)
    c: Weight(g193) = 1
    c: Equal(g193,g194)
    c: Equal(g193,g195)
    c: InternalAlignment(g193,g196)
    c: InternalAlignment(g194,g196)
    c: InternalAlignment(g195,g196)
    c: InternalAlignment(g197,g196)
    c: InternalAlignment(g198,g196)
    c: Weight(g199) = 1
    c: Equal(g199,g200)
    c: Equal(g199,g201)
    c: InternalAlignment(g199,g202)
    c: InternalAlignment(g200,g202)
    c: InternalAlignment(g201,g202)
    c: InternalAlignment(g203,g202)
    c: InternalAlignment(g204,g202)
    c: Block(g202)
    c: Block(g196)
    c: Coincident(g205,g202)
    c: Coincident(g205,g37)
    c: Coincident(g206,g37)
    c: Coincident(g206,g196)
    c: Coincident(g207,g196)
    c: Coincident(g207,g202)
    c: Vertical(g207)
    c: Weight(g208) = 1
    c: Equal(g208,g209)
    c: Equal(g208,g210)
    c: InternalAlignment(g208,g211)
    c: InternalAlignment(g209,g211)
    c: InternalAlignment(g210,g211)
    c: InternalAlignment(g212,g211)
    c: InternalAlignment(g213,g211)
    c: Weight(g214) = 1
    c: Equal(g214,g215)
    c: Equal(g214,g216)
    c: InternalAlignment(g214,g217)
    c: InternalAlignment(g215,g217)
    c: InternalAlignment(g216,g217)
    c: InternalAlignment(g218,g217)
    c: InternalAlignment(g219,g217)
    c: Block(g217)
    c: Block(g211)
    c: Coincident(g220,g211)
    c: Coincident(g220,g43)
    c: Coincident(g221,g43)
    c: Coincident(g221,g217)
    c: Coincident(g222,g217)
    c: Coincident(g222,g211)
    c: Vertical(g222)
    c: Horizontal(g223)
    c: Block(g223)
    c: Vertical(g224)
    c: Block(g224)
    c: Block(g225)
    c: Weight(g226) = 1
    c: Equal(g226,g227)
    c: Equal(g226,g228)
    c: InternalAlignment(g226,g229)
    c: InternalAlignment(g227,g229)
    c: InternalAlignment(g228,g229)
    c: InternalAlignment(g230,g229)
    c: InternalAlignment(g231,g229)
    c: Weight(g232) = 1
    c: Equal(g232,g233)
    c: Equal(g232,g234)
    c: InternalAlignment(g232,g235)
    c: InternalAlignment(g233,g235)
    c: InternalAlignment(g234,g235)
    c: InternalAlignment(g236,g235)
    c: InternalAlignment(g237,g235)
    c: Weight(g238) = 1
    c: Equal(g238,g239)
    c: Equal(g238,g240)
    c: InternalAlignment(g238,g241)
    c: InternalAlignment(g239,g241)
    c: InternalAlignment(g240,g241)
    c: InternalAlignment(g242,g241)
    c: InternalAlignment(g243,g241)
    c: Weight(g244) = 1
    c: Equal(g244,g245)
    c: Equal(g244,g246)
    c: InternalAlignment(g244,g247)
    c: InternalAlignment(g245,g247)
    c: InternalAlignment(g246,g247)
    c: InternalAlignment(g248,g247)
    c: InternalAlignment(g249,g247)
    c: Block(g229)
    c: Block(g235)
    c: Block(g241)
    c: Block(g247)
    c: Coincident(g250,g235)
    c: Coincident(g250,g229)
    c: Horizontal(g250)
    c: Block(g192)
    c: Weight(g251) = 1
    c: Equal(g251,g252)
    c: Equal(g251,g253)
    c: InternalAlignment(g251,g254)
    c: InternalAlignment(g252,g254)
    c: InternalAlignment(g253,g254)
    c: InternalAlignment(g255,g254)
    c: InternalAlignment(g256,g254)
    c: Weight(g257) = 1
    c: Equal(g257,g258)
    c: Equal(g257,g259)
    c: InternalAlignment(g257,g260)
    c: InternalAlignment(g258,g260)
    c: InternalAlignment(g259,g260)
    c: InternalAlignment(g261,g260)
    c: InternalAlignment(g262,g260)
    c: Block(g254)
    c: Block(g260)
    c: Coincident(g263,g254)
    c: Coincident(g263,g260)
    c: Weight(g264) = 1
    c: Equal(g264,g265)
    c: Equal(g264,g266)
    c: InternalAlignment(g264,g267)
    c: InternalAlignment(g265,g267)
    c: InternalAlignment(g266,g267)
    c: InternalAlignment(g268,g267)
    c: InternalAlignment(g269,g267)
    c: Weight(g270) = 1
    c: Equal(g270,g271)
    c: Equal(g270,g272)
    c: InternalAlignment(g270,g273)
    c: InternalAlignment(g271,g273)
    c: InternalAlignment(g272,g273)
    c: InternalAlignment(g274,g273)
    c: InternalAlignment(g275,g273)
    c: Weight(g276) = 1
    c: Equal(g276,g277)
    c: Equal(g276,g278)
    c: InternalAlignment(g276,g279)
    c: InternalAlignment(g277,g279)
    c: InternalAlignment(g278,g279)
    c: InternalAlignment(g280,g279)
    c: InternalAlignment(g281,g279)
    c: Block(g279)
    c: Block(g273)
    c: Block(g267)
    c: Coincident(g282,g273)
    c: Coincident(g282,g267)
    c: Coincident(g283,g267)
    c: Coincident(g283,g279)
    c: Vertical(g283)
    c: Coincident(g284,g279)
    c: Coincident(g284,g273)
    c: Horizontal(g284)
    c: Weight(g285) = 1
    c: Equal(g285,g286)
    c: InternalAlignment(g285,g287)
    c: InternalAlignment(g286,g287)
    c: InternalAlignment(g288,g287)
    c: InternalAlignment(g289,g287)
    c: Weight(g290) = 1
    c: InternalAlignment(g291,g293)
    c: InternalAlignment(g292,g293)
    c: InternalAlignment(g294,g293)
    c: InternalAlignment(g295,g293)
    c: Weight(g296) = 1
    c: Equal(g296,g297)
    c: Equal(g296,g298)
    c: InternalAlignment(g296,g299)
    c: InternalAlignment(g297,g299)
    c: InternalAlignment(g298,g299)
    c: InternalAlignment(g300,g299)
    c: InternalAlignment(g301,g299)
    c: Equal(g302,g303)
    c: Equal(g302,g304)
    c: InternalAlignment(g302,g305)
    c: InternalAlignment(g303,g305)
    c: InternalAlignment(g304,g305)
    c: InternalAlignment(g306,g305)
    c: InternalAlignment(g307,g305)
    c: Block(g293)
    c: Block(g299)
    c: Block(g305)
    c: Block(g287)
    c: Coincident(g308,g287)
    c: Coincident(g308,g293)
    c: Horizontal(g308)
    c: Coincident(g309,g293)
    c: Coincident(g309,g299)
    c: Vertical(g309)
    c: Coincident(g310,g299)
    c: Coincident(g310,g305)
    c: Horizontal(g310)
    c: Coincident(g311,g305)
    c: Coincident(g311,g287)
    c: Weight(g312) = 1
    c: Equal(g312,g313)
    c: Equal(g312,g314)
    c: InternalAlignment(g312,g315)
    c: InternalAlignment(g313,g315)
    c: InternalAlignment(g314,g315)
    c: InternalAlignment(g316,g315)
    c: InternalAlignment(g317,g315)
    c: Weight(g318) = 1
    c: Equal(g318,g319)
    c: Equal(g318,g320)
    c: InternalAlignment(g318,g321)
    c: InternalAlignment(g319,g321)
    c: InternalAlignment(g320,g321)
    c: InternalAlignment(g322,g321)
    c: InternalAlignment(g323,g321)
    c: Weight(g324) = 1
    c: Equal(g324,g325)
    c: Equal(g324,g326)
    c: InternalAlignment(g324,g327)
    c: InternalAlignment(g325,g327)
    c: InternalAlignment(g326,g327)
    c: InternalAlignment(g328,g327)
    c: InternalAlignment(g329,g327)
    c: Block(g327)
    c: Block(g321)
    c: Block(g315)
    c: Coincident(g330,g327)
    c: Coincident(g330,g321)
    c: Horizontal(g330)
    c: Coincident(g331,g321)
    c: Coincident(g331,g315)
    c: Vertical(g331)
    c: Coincident(g332,g315)
    c: Coincident(g332,g327)
    c: InternalAlignment(g333,g334)
    c: InternalAlignment(g335,g334)
    c: InternalAlignment(g336,g334)
    c: Block(g334)
    c: Equal(g337,g338)
    c: Equal(g337,g339)
    c: InternalAlignment(g337,g340)
    c: InternalAlignment(g338,g340)
    c: InternalAlignment(g339,g340)
    c: InternalAlignment(g341,g340)
    c: InternalAlignment(g342,g340)
    c: Block(g340)
    c: Coincident(g343,g334)
    c: Horizontal(g343)
    c: Block(g343)
    c: Coincident(g344,g334)
    c: Coincident(g344,g260)
    c: Vertical(g344)
    c: Coincident(g345,g340)
    c: Coincident(g345,g254)
    c: Vertical(g345)
    c: Coincident(g347,g5)
    c: Coincident(g348,g5)
    c: Block(g346)
    c: Block(g5)
    c: Block(g348)
    c: Block(g347)
    c: Distance(g344) = 119.89
FEATURE [Sketcher::SketchObject] Sketch001
  FullyConstrained = true
  MapMode = 4
  Placement = pos=(0,0,0) rot=(0.57735,0.57735,0.57735;2.0944rad)
  Support = -> [Sketch]
  sketch-geometry (46):
    g0: BSplineCurve PolesCount=3 KnotsCount=2 Degree=2 IsPeriodic=0
    g1: ArcOfCircle CenterX=73.1223 CenterY=-32.291 CenterZ=0 NormalX=0 NormalY=0 NormalZ=1 AngleXU=0 Radius=13 StartAngle=5.92268 EndAngle=9.06428
    g2: ArcOfCircle CenterX=66.7816 CenterY=-49.1439 CenterZ=0 NormalX=0 NormalY=0 NormalZ=1 AngleXU=0 Radius=13 StartAngle=2.78068 EndAngle=5.92131
    g3: ArcOfCircle CenterX=55.9263 CenterY=-78.1807 CenterZ=0 NormalX=0 NormalY=0 NormalZ=1 AngleXU=0 Radius=13 StartAngle=5.92268 EndAngle=9.06428
    g4: ArcOfCircle CenterX=49.5884 CenterY=-95.0342 CenterZ=0 NormalX=0 NormalY=0 NormalZ=1 AngleXU=0 Radius=13 StartAngle=2.78068 EndAngle=5.92131
    g5: ArcOfCircle CenterX=38.7206 CenterY=-124.067 CenterZ=0 NormalX=0 NormalY=0 NormalZ=1 AngleXU=0 Radius=13 StartAngle=5.92268 EndAngle=9.06428
    g6: ArcOfCircle CenterX=32.3875 CenterY=-140.92 CenterZ=0 NormalX=0 NormalY=0 NormalZ=1 AngleXU=0 Radius=13 StartAngle=2.78068 EndAngle=5.92131
    g7: ArcOfCircle CenterX=21.4715 CenterY=-169.934 CenterZ=0 NormalX=0 NormalY=0 NormalZ=1 AngleXU=0 Radius=13 StartAngle=5.92268 EndAngle=9.06428
    g8: ArcOfCircle CenterX=15.1336 CenterY=-186.787 CenterZ=0 NormalX=0 NormalY=0 NormalZ=1 AngleXU=0 Radius=13 StartAngle=2.78068 EndAngle=5.92131
    g9-g12: Circle x4 (B-spline internal-alignment scaffolding for g13; pole/knot coordinates omitted)
    g13: BSplineCurve PolesCount=4 KnotsCount=2 Degree=3 IsPeriodic=0
    g14: GeomPoint X=28.8094 Y=-19.0875 Z=0
    g15: GeomPoint X=47.0443 Y=-50.4712 Z=0
    g16: Circle CenterX=53.5586 CenterY=-23.2695 CenterZ=0 NormalX=0 NormalY=0 NormalZ=1 AngleXU=0 Radius=3.24518
    g17: Circle CenterX=-195.441 CenterY=-127.082 CenterZ=0 NormalX=0 NormalY=0 NormalZ=1 AngleXU=0 Radius=1
    g18: Circle CenterX=-8.24091 CenterY=-197.481 CenterZ=0 NormalX=0 NormalY=0 NormalZ=1 AngleXU=0 Radius=1
    g19: Circle CenterX=12.8789 CenterY=-141.321 CenterZ=0 NormalX=0 NormalY=0 NormalZ=1 AngleXU=0 Radius=1
    g20: BSplineCurve PolesCount=3 KnotsCount=2 Degree=2 IsPeriodic=0
    g21: GeomPoint X=-195.441 Y=-127.082 Z=0
    g22: GeomPoint X=12.8789 Y=-141.321 Z=0
    g23: Circle CenterX=-12.8016 CenterY=-179.036 CenterZ=0 NormalX=0 NormalY=0 NormalZ=1 AngleXU=0 Radius=10.5072
    g24: Circle CenterX=0.933922 CenterY=-166.43 CenterZ=0 NormalX=0 NormalY=0 NormalZ=1 AngleXU=0 Radius=3.26661
    g25: Circle CenterX=-33.5518 CenterY=-176.44 CenterZ=0 NormalX=0 NormalY=0 NormalZ=1 AngleXU=0 Radius=5.64388
    g26: Circle CenterX=-47.2366 CenterY=-173.859 CenterZ=0 NormalX=0 NormalY=0 NormalZ=1 AngleXU=0 Radius=3.01653
    g27: Circle CenterX=-56.2595 CenterY=-171.456 CenterZ=0 NormalX=0 NormalY=0 NormalZ=1 AngleXU=0 Radius=2.12826
    g28: ArcOfCircle CenterX=51.2151 CenterY=-198.473 CenterZ=0 NormalX=0 NormalY=0 NormalZ=1 AngleXU=0 Radius=20 StartAngle=2.78189 EndAngle=4.35269
    g29: LineSegment StartX=32.4951 StartY=-191.433 StartZ=0 EndX=94.6578 EndY=-26.1352 EndZ=0
    g30: LineSegment StartX=43.1192 StartY=-220.001 StartZ=0 EndX=-196.497 EndY=-129.89 EndZ=0
    g31: LineSegment StartX=43.1192 StartY=-220.001 StartZ=0 EndX=44.1752 EndY=-217.193 EndZ=0
    g32: LineSegment StartX=117.223 StartY=-19.0875 StartZ=0 EndX=117.223 EndY=-16.0875 EndZ=0
    g33: LineSegment StartX=117.223 StartY=-16.0875 StartZ=0 EndX=17.2232 EndY=-16.0875 EndZ=0
    g34: LineSegment StartX=17.2232 StartY=-16.0875 StartZ=0 EndX=17.2232 EndY=-19.0875 EndZ=0
    g35: LineSegment StartX=28.8094 StartY=-19.0875 StartZ=0 EndX=17.2232 EndY=-19.0875 EndZ=0
    g36: LineSegment StartX=47.0443 StartY=-50.4712 StartZ=0 EndX=12.8789 EndY=-141.321 EndZ=0
    g37: LineSegment StartX=-195.441 StartY=-127.082 StartZ=0 EndX=-196.497 EndY=-129.89 EndZ=0
    g38: LineSegment StartX=85.2866 StartY=-36.8766 StartZ=0 EndX=78.9396 EndY=-53.7463 EndZ=0
    g39: LineSegment StartX=60.9579 StartY=-27.7053 StartZ=0 EndX=54.6191 EndY=-44.5532 EndZ=0
    g40: LineSegment StartX=68.0907 StartY=-82.7664 StartZ=0 EndX=61.7465 EndY=-99.6365 EndZ=0
    g41: LineSegment StartX=43.7619 StartY=-73.595 StartZ=0 EndX=37.426 EndY=-90.4435 EndZ=0
    g42: LineSegment StartX=50.885 StartY=-128.652 StartZ=0 EndX=44.5456 EndY=-145.522 EndZ=0
    g43: LineSegment StartX=26.5562 StartY=-119.481 StartZ=0 EndX=20.2251 EndY=-136.329 EndZ=0
    g44: LineSegment StartX=9.3071 StartY=-165.349 StartZ=0 EndX=2.97115 EndY=-182.197 EndZ=0
    g45: LineSegment StartX=33.6358 StartY=-174.52 StartZ=0 EndX=27.2917 EndY=-191.39 EndZ=0
  constraints (71):
    c: Block(g0)
    c: Block(g1)
    c: Block(g2)
    c: Block(g4)
    c: Block(g3)
    c: Block(g6)
    c: Block(g5)
    c: Block(g8)
    c: Block(g7)
    c: Weight(g9) = 1
    c: Equal(g9,g10)
    c: Equal(g9,g11)
    c: Equal(g9,g12)
    c: InternalAlignment(g9-g12 -> g13) x4
    c: InternalAlignment(g14,g13)
    c: InternalAlignment(g15,g13)
    c: Block(g16)
    c: Weight(g17) = 1
    c: Equal(g17,g18)
    c: Equal(g17,g19)
    c: InternalAlignment(g17,g20)
    c: InternalAlignment(g18,g20)
    c: InternalAlignment(g19,g20)
    c: InternalAlignment(g21,g20)
    c: InternalAlignment(g22,g20)
    c: Block(g20)
    c: Block(g23)
    c: Block(g24)
    c: Block(g25)
    c: Block(g26)
    c: Block(g27)
    c: Block(g28)
    c: Coincident(g29,g28)
    c: Coincident(g29,g0)
    c: Block(g13)
    c: Coincident(g31,g30)
    c: Coincident(g31,g28)
    c: Block(g31)
    c: Coincident(g32,g0)
    c: Vertical(g32)
    c: Coincident(g33,g32)
    c: Horizontal(g33)
    c: Coincident(g34,g33)
    c: Vertical(g34)
    c: Block(g33)
    c: Coincident(g35,g13)
    c: Coincident(g35,g34)
    c: Horizontal(g35)
    c: Coincident(g36,g13)
    c: Coincident(g36,g20)
    c: Coincident(g37,g20)
    c: Coincident(g37,g30)
    c: Block(g30)
    c: Coincident(g38,g1)
    c: Coincident(g38,g2)
    c: Coincident(g39,g1)
    c: Coincident(g39,g2)
    c: Coincident(g40,g3)
    c: Coincident(g40,g4)
    c: Coincident(g41,g3)
    c: Coincident(g41,g4)
    c: Coincident(g42,g5)
    c: Coincident(g42,g6)
    c: Coincident(g43,g5)
    c: Coincident(g43,g6)
    c: Coincident(g44,g7)
    c: Coincident(g44,g8)
    c: Coincident(g45,g7)
    c: Coincident(g45,g8)
    c: Distance(g30) = 256
    c: Distance(g33) = 100
FEATURE [Part::Extrusion] Extrude002
  Base = -> Sketch001
  Dir = (1,0,0)
  DirMode = 2
  FaceMakerClass = Part::FaceMakerBullseye
  LengthFwd = 8
  LengthRev = 0
  Solid = true
  Symmetric = false
FEATURE [Sketcher::SketchObject] Sketch002
  FullyConstrained = true
  sketch-geometry (20):
    g0: LineSegment StartX=-2.77179 StartY=-200.304 StartZ=0 EndX=5.22821 EndY=-200.304 EndZ=0
    g1: LineSegment StartX=5.22821 StartY=-200.304 StartZ=0 EndX=5.22821 EndY=-197.304 EndZ=0
    g2: LineSegment StartX=-2.77179 StartY=-200.304 StartZ=0 EndX=-2.77179 EndY=-197.304 EndZ=0
    g3: LineSegment StartX=5.22821 StartY=-197.304 StartZ=0 EndX=8.22821 EndY=-197.304 EndZ=0
    g4: LineSegment StartX=-2.77179 StartY=-197.304 StartZ=0 EndX=-5.77179 EndY=-197.304 EndZ=0
    g5: LineSegment StartX=19.2282 StartY=-203.304 StartZ=0 EndX=19.2282 EndY=-206.304 EndZ=0
    g6: LineSegment StartX=-16.7718 StartY=-203.304 StartZ=0 EndX=-16.7718 EndY=-206.304 EndZ=0
    g7: LineSegment StartX=-16.7718 StartY=-206.304 StartZ=0 EndX=19.2282 EndY=-206.304 EndZ=0
    g8: Circle CenterX=-16.7718 CenterY=-203.304 CenterZ=0 NormalX=0 NormalY=0 NormalZ=1 AngleXU=0 Radius=1
    g9: Circle CenterX=-5.77179 CenterY=-203.304 CenterZ=0 NormalX=0 NormalY=0 NormalZ=1 AngleXU=0 Radius=1
    g10: Circle CenterX=-5.77179 CenterY=-197.304 CenterZ=0 NormalX=0 NormalY=0 NormalZ=1 AngleXU=0 Radius=1
    g11: BSplineCurve PolesCount=3 KnotsCount=2 Degree=2 IsPeriodic=0
    g12: GeomPoint X=-16.7718 Y=-203.304 Z=0
    g13: GeomPoint X=-5.77179 Y=-197.304 Z=0
    g14: Circle CenterX=19.2282 CenterY=-203.304 CenterZ=0 NormalX=0 NormalY=0 NormalZ=1 AngleXU=0 Radius=1
    g15: Circle CenterX=8.22821 CenterY=-203.304 CenterZ=0 NormalX=0 NormalY=0 NormalZ=1 AngleXU=0 Radius=1
    g16: Circle CenterX=8.22821 CenterY=-197.304 CenterZ=0 NormalX=0 NormalY=0 NormalZ=1 AngleXU=0 Radius=1
    g17: BSplineCurve PolesCount=3 KnotsCount=2 Degree=2 IsPeriodic=0
    g18: GeomPoint X=19.2282 Y=-203.304 Z=0
    g19: GeomPoint X=8.22821 Y=-197.304 Z=0
  constraints (41):
    c: Horizontal(g0)
    c: Distance(g0) = 8
    c: Coincident(g1,g0)
    c: Vertical(g1)
    c: Distance(g1) = 3
    c: Coincident(g2,g0)
    c: Vertical(g2)
    c: Distance(g2) = 3
    c: Coincident(g3,g1)
    c: Horizontal(g3)
    c: Distance(g3) = 3
    c: Coincident(g4,g2)
    c: Horizontal(g4)
    c: Distance(g4) = 3
    c: Vertical(g5)
    c: Vertical(g6)
    c: Coincident(g7,g6)
    c: Coincident(g7,g5)
    c: Weight(g8) = 1
    c: Equal(g8,g9)
    c: Equal(g8,g10)
    c: Coincident(g11,g4)
    c: InternalAlignment(g8,g11)
    c: InternalAlignment(g9,g11)
    c: InternalAlignment(g10,g11)
    c: InternalAlignment(g12,g11)
    c: InternalAlignment(g13,g11)
    c: Coincident(g17,g5)
    c: Weight(g14) = 1
    c: Equal(g14,g15)
    c: Equal(g14,g16)
    c: Coincident(g17,g3)
    c: InternalAlignment(g14,g17)
    c: InternalAlignment(g15,g17)
    c: InternalAlignment(g16,g17)
    c: InternalAlignment(g18,g17)
    c: InternalAlignment(g19,g17)
    c: Block(g7)
    c: Block(g17)
    c: Block(g11)
    c: Block(g6)
FEATURE [Part::Extrusion] Extrude003
  Base = -> Sketch002
  Dir = (0,0,1)
  DirMode = 2
  FaceMakerClass = Part::FaceMakerBullseye
  LengthFwd = 260
  LengthRev = 0
  Solid = true
  Symmetric = false
FEATURE [Sketcher::SketchObject] Sketch003
  FullyConstrained = false
  sketch-geometry (398):
    g0: LineSegment StartX=-42.9272 StartY=136.221 StartZ=0 EndX=-42.9272 EndY=-103.779 EndZ=0
    g1: LineSegment StartX=407.073 StartY=136.221 StartZ=0 EndX=407.073 EndY=-103.779 EndZ=0
    g2: ArcOfCircle CenterX=-26.9272 CenterY=-83.7794 CenterZ=0 NormalX=0 NormalY=0 NormalZ=1 AngleXU=0 Radius=8 StartAngle=3.14159 EndAngle=6.28319
    g3: ArcOfCircle CenterX=391.073 CenterY=-83.7794 CenterZ=0 NormalX=0 NormalY=0 NormalZ=1 AngleXU=0 Radius=8 StartAngle=3.14159 EndAngle=6.28319
    g4: Circle CenterX=175.022 CenterY=27.0628 CenterZ=0 NormalX=0 NormalY=0 NormalZ=1 AngleXU=0 Radius=1
    g5: Circle CenterX=179.022 CenterY=24.8665 CenterZ=0 NormalX=0 NormalY=0 NormalZ=1 AngleXU=0 Radius=1
    g6: Circle CenterX=179.022 CenterY=27.0628 CenterZ=0 NormalX=0 NormalY=0 NormalZ=1 AngleXU=0 Radius=1
    g7: BSplineCurve PolesCount=3 KnotsCount=2 Degree=2 IsPeriodic=0
    g8: GeomPoint X=175.022 Y=27.0628 Z=0
    g9: GeomPoint X=179.022 Y=27.0628 Z=0
    g10: Circle CenterX=189.124 CenterY=27.0628 CenterZ=0 NormalX=0 NormalY=0 NormalZ=1 AngleXU=0 Radius=1
    g11: Circle CenterX=185.124 CenterY=24.8665 CenterZ=0 NormalX=0 NormalY=0 NormalZ=1 AngleXU=0 Radius=1
    g12: Circle CenterX=185.124 CenterY=27.0628 CenterZ=0 NormalX=0 NormalY=0 NormalZ=1 AngleXU=0 Radius=1
    g13: BSplineCurve PolesCount=3 KnotsCount=2 Degree=2 IsPeriodic=0
    g14: GeomPoint X=189.124 Y=27.0628 Z=0
    g15: GeomPoint X=185.124 Y=27.0628 Z=0
    g16: Circle CenterX=175.022 CenterY=5.37834 CenterZ=0 NormalX=0 NormalY=0 NormalZ=1 AngleXU=0 Radius=1
    g17: Circle CenterX=179.022 CenterY=7.57463 CenterZ=0 NormalX=0 NormalY=0 NormalZ=1 AngleXU=0 Radius=1
    g18: Circle CenterX=179.022 CenterY=5.34704 CenterZ=0 NormalX=0 NormalY=0 NormalZ=1 AngleXU=0 Radius=1
    g19: BSplineCurve PolesCount=3 KnotsCount=2 Degree=2 IsPeriodic=0
    g20: GeomPoint X=175.022 Y=5.37834 Z=0
    g21: GeomPoint X=179.022 Y=5.34704 Z=0
    g22: Circle CenterX=189.124 CenterY=5.37834 CenterZ=0 NormalX=0 NormalY=0 NormalZ=1 AngleXU=0 Radius=1
    g23: Circle CenterX=185.124 CenterY=7.57463 CenterZ=0 NormalX=0 NormalY=0 NormalZ=1 AngleXU=0 Radius=1
    g24: Circle CenterX=185.124 CenterY=5.34704 CenterZ=0 NormalX=0 NormalY=0 NormalZ=1 AngleXU=0 Radius=1
    g25: BSplineCurve PolesCount=3 KnotsCount=2 Degree=2 IsPeriodic=0
    g26: GeomPoint X=189.124 Y=5.37834 Z=0
    g27: GeomPoint X=185.124 Y=5.34704 Z=0
    g28: Circle CenterX=165.871 CenterY=18.1458 CenterZ=0 NormalX=0 NormalY=0 NormalZ=1 AngleXU=0 Radius=1
    g29: Circle CenterX=169.377 CenterY=16.2206 CenterZ=0 NormalX=0 NormalY=0 NormalZ=1 AngleXU=0 Radius=1
    g30: Circle CenterX=165.871 CenterY=14.2954 CenterZ=0 NormalX=0 NormalY=0 NormalZ=1 AngleXU=0 Radius=1
    g31: BSplineCurve PolesCount=3 KnotsCount=2 Degree=2 IsPeriodic=0
    g32: GeomPoint X=165.871 Y=18.1458 Z=0
    g33: GeomPoint X=165.871 Y=14.2954 Z=0
    g34: Circle CenterX=198.275 CenterY=18.1458 CenterZ=0 NormalX=0 NormalY=0 NormalZ=1 AngleXU=0 Radius=1
    g35: Circle CenterX=194.768 CenterY=16.2206 CenterZ=0 NormalX=0 NormalY=0 NormalZ=1 AngleXU=0 Radius=1
    g36: Circle CenterX=198.275 CenterY=14.2954 CenterZ=0 NormalX=0 NormalY=0 NormalZ=1 AngleXU=0 Radius=1
    g37: BSplineCurve PolesCount=3 KnotsCount=2 Degree=2 IsPeriodic=0
    g38: GeomPoint X=198.275 Y=18.1458 Z=0
    g39: GeomPoint X=198.275 Y=14.2954 Z=0
    g40: LineSegment StartX=407.073 StartY=-103.779 StartZ=0 EndX=-42.9272 EndY=-103.779 EndZ=0
    g41: Circle CenterX=125.607 CenterY=54.1951 CenterZ=0 NormalX=0 NormalY=0 NormalZ=1 AngleXU=0 Radius=1
    g42: Circle CenterX=139.632 CenterY=46.4944 CenterZ=0 NormalX=0 NormalY=0 NormalZ=1 AngleXU=0 Radius=1
    g43: Circle CenterX=127.326 CenterY=56.7187 CenterZ=0 NormalX=0 NormalY=0 NormalZ=1 AngleXU=0 Radius=1
    g44: BSplineCurve PolesCount=3 KnotsCount=2 Degree=2 IsPeriodic=0
    g45: GeomPoint X=125.607 Y=54.1951 Z=0
    g46: GeomPoint X=127.326 Y=56.7187 Z=0
    g47: Circle CenterX=236.821 CenterY=56.7187 CenterZ=0 NormalX=0 NormalY=0 NormalZ=1 AngleXU=0 Radius=1
    g48: Circle CenterX=224.513 CenterY=46.4944 CenterZ=0 NormalX=0 NormalY=0 NormalZ=1 AngleXU=0 Radius=1
    g49: Circle CenterX=238.538 CenterY=54.1951 CenterZ=0 NormalX=0 NormalY=0 NormalZ=1 AngleXU=0 Radius=1
    g50: BSplineCurve PolesCount=3 KnotsCount=2 Degree=2 IsPeriodic=0
    g51: GeomPoint X=236.821 Y=56.7187 Z=0
    g52: GeomPoint X=238.538 Y=54.1951 Z=0
    g53: Circle CenterX=238.538 CenterY=-21.7539 CenterZ=0 NormalX=0 NormalY=0 NormalZ=1 AngleXU=0 Radius=1
    g54: Circle CenterX=224.513 CenterY=-14.0532 CenterZ=0 NormalX=0 NormalY=0 NormalZ=1 AngleXU=0 Radius=1
    g55: Circle CenterX=236.821 CenterY=-24.2775 CenterZ=0 NormalX=0 NormalY=0 NormalZ=1 AngleXU=0 Radius=1
    g56: BSplineCurve PolesCount=3 KnotsCount=2 Degree=2 IsPeriodic=0
    g57: GeomPoint X=238.538 Y=-21.7539 Z=0
    g58: GeomPoint X=236.821 Y=-24.2775 Z=0
    g59: Circle CenterX=125.607 CenterY=-21.7539 CenterZ=0 NormalX=0 NormalY=0 NormalZ=1 AngleXU=0 Radius=1
    g60: Circle CenterX=139.632 CenterY=-14.0532 CenterZ=0 NormalX=0 NormalY=0 NormalZ=1 AngleXU=0 Radius=1
    g61: Circle CenterX=127.325 CenterY=-24.2775 CenterZ=0 NormalX=0 NormalY=0 NormalZ=1 AngleXU=0 Radius=1
    g62: BSplineCurve PolesCount=3 KnotsCount=2 Degree=2 IsPeriodic=0
    g63: GeomPoint X=125.607 Y=-21.7539 Z=0
    g64: GeomPoint X=127.325 Y=-24.2775 Z=0
    g65: Circle CenterX=302.996 CenterY=111.695 CenterZ=0 NormalX=0 NormalY=0 NormalZ=1 AngleXU=0 Radius=1
    g66: Circle CenterX=306.073 CenterY=114.251 CenterZ=0 NormalX=0 NormalY=0 NormalZ=1 AngleXU=0 Radius=1
    g67: Circle CenterX=306.073 CenterY=110.251 CenterZ=0 NormalX=0 NormalY=0 NormalZ=1 AngleXU=0 Radius=1
    g68: BSplineCurve PolesCount=3 KnotsCount=2 Degree=2 IsPeriodic=0
    g69: GeomPoint X=302.996 Y=111.695 Z=0
    g70: GeomPoint X=306.073 Y=110.251 Z=0
    g71: Circle CenterX=306.073 CenterY=95.2763 CenterZ=0 NormalX=0 NormalY=0 NormalZ=1 AngleXU=0 Radius=1
    g72: Circle CenterX=306.073 CenterY=91.2763 CenterZ=0 NormalX=0 NormalY=0 NormalZ=1 AngleXU=0 Radius=1
    g73: Circle CenterX=302.567 CenterY=89.3511 CenterZ=0 NormalX=0 NormalY=0 NormalZ=1 AngleXU=0 Radius=1
    g74: BSplineCurve PolesCount=3 KnotsCount=2 Degree=2 IsPeriodic=0
    g75: GeomPoint X=306.073 Y=95.2763 Z=0
    g76: GeomPoint X=302.567 Y=89.3511 Z=0
    g77: LineSegment StartX=306.073 StartY=110.251 StartZ=0 EndX=306.073 EndY=95.2763 EndZ=0
    g78: LineSegment StartX=302.996 StartY=111.695 StartZ=0 EndX=236.821 EndY=56.7187 EndZ=0
    g79: LineSegment StartX=238.538 StartY=54.1951 StartZ=0 EndX=302.567 EndY=89.3511 EndZ=0
    g80: Circle CenterX=61.1496 CenterY=111.695 CenterZ=0 NormalX=0 NormalY=0 NormalZ=1 AngleXU=0 Radius=1
    g81: Circle CenterX=58.0728 CenterY=114.251 CenterZ=0 NormalX=0 NormalY=0 NormalZ=1 AngleXU=0 Radius=1
    g82: Circle CenterX=58.0728 CenterY=110.251 CenterZ=0 NormalX=0 NormalY=0 NormalZ=1 AngleXU=0 Radius=1
    g83: BSplineCurve PolesCount=3 KnotsCount=2 Degree=2 IsPeriodic=0
    g84: GeomPoint X=61.1496 Y=111.695 Z=0
    g85: GeomPoint X=58.0728 Y=110.251 Z=0
    g86: Circle CenterX=61.5791 CenterY=89.3511 CenterZ=0 NormalX=0 NormalY=0 NormalZ=1 AngleXU=0 Radius=1
    g87: Circle CenterX=58.0728 CenterY=91.2763 CenterZ=0 NormalX=0 NormalY=0 NormalZ=1 AngleXU=0 Radius=1
    g88: Circle CenterX=58.0728 CenterY=95.2763 CenterZ=0 NormalX=0 NormalY=0 NormalZ=1 AngleXU=0 Radius=1
    g89: BSplineCurve PolesCount=3 KnotsCount=2 Degree=2 IsPeriodic=0
    g90: GeomPoint X=61.5791 Y=89.3511 Z=0
    g91: GeomPoint X=58.0728 Y=95.2763 Z=0
    g92: LineSegment StartX=58.0728 StartY=110.251 StartZ=0 EndX=58.0728 EndY=95.2763 EndZ=0
    g93: LineSegment StartX=61.1496 StartY=111.695 StartZ=0 EndX=127.326 EndY=56.7187 EndZ=0
    g94: LineSegment StartX=125.607 StartY=54.1951 StartZ=0 EndX=61.5791 EndY=89.3511 EndZ=0
    g95: Circle CenterX=61.5791 CenterY=-56.9099 CenterZ=0 NormalX=0 NormalY=0 NormalZ=1 AngleXU=0 Radius=1
    g96: Circle CenterX=58.0728 CenterY=-58.8351 CenterZ=0 NormalX=0 NormalY=0 NormalZ=1 AngleXU=0 Radius=1
    g97: Circle CenterX=58.0728 CenterY=-62.8351 CenterZ=0 NormalX=0 NormalY=0 NormalZ=1 AngleXU=0 Radius=1
    g98: BSplineCurve PolesCount=3 KnotsCount=2 Degree=2 IsPeriodic=0
    g99: GeomPoint X=61.5791 Y=-56.9099 Z=0
    g100: GeomPoint X=58.0728 Y=-62.8351 Z=0
    g101: Circle CenterX=58.0728 CenterY=-77.8102 CenterZ=0 NormalX=0 NormalY=0 NormalZ=1 AngleXU=0 Radius=1
    g102: Circle CenterX=58.0728 CenterY=-81.8102 CenterZ=0 NormalX=0 NormalY=0 NormalZ=1 AngleXU=0 Radius=1
    g103: Circle CenterX=61.1496 CenterY=-79.2541 CenterZ=0 NormalX=0 NormalY=0 NormalZ=1 AngleXU=0 Radius=1
    g104: BSplineCurve PolesCount=3 KnotsCount=2 Degree=2 IsPeriodic=0
    g105: GeomPoint X=58.0728 Y=-77.8102 Z=0
    g106: GeomPoint X=61.1496 Y=-79.2541 Z=0
    g107: LineSegment StartX=58.0728 StartY=-62.8351 StartZ=0 EndX=58.0728 EndY=-77.8102 EndZ=0
    g108: LineSegment StartX=61.1496 StartY=-79.2541 StartZ=0 EndX=127.325 EndY=-24.2775 EndZ=0
    g109: LineSegment StartX=125.607 StartY=-21.7539 StartZ=0 EndX=61.5791 EndY=-56.9099 EndZ=0
    g110: Circle CenterX=302.567 CenterY=-56.9099 CenterZ=0 NormalX=0 NormalY=0 NormalZ=1 AngleXU=0 Radius=1
    g111: Circle CenterX=306.073 CenterY=-58.8351 CenterZ=0 NormalX=0 NormalY=0 NormalZ=1 AngleXU=0 Radius=1
    g112: Circle CenterX=306.073 CenterY=-62.8351 CenterZ=0 NormalX=0 NormalY=0 NormalZ=1 AngleXU=0 Radius=1
    g113: BSplineCurve PolesCount=3 KnotsCount=2 Degree=2 IsPeriodic=0
    g114: GeomPoint X=302.567 Y=-56.9099 Z=0
    g115: GeomPoint X=306.073 Y=-62.8351 Z=0
    g116: Circle CenterX=302.996 CenterY=-79.2541 CenterZ=0 NormalX=0 NormalY=0 NormalZ=1 AngleXU=0 Radius=1
    g117: Circle CenterX=306.073 CenterY=-81.8102 CenterZ=0 NormalX=0 NormalY=0 NormalZ=1 AngleXU=0 Radius=1
    g118: Circle CenterX=306.073 CenterY=-77.8102 CenterZ=0 NormalX=0 NormalY=0 NormalZ=1 AngleXU=0 Radius=1
    g119: BSplineCurve PolesCount=3 KnotsCount=2 Degree=2 IsPeriodic=0
    g120: GeomPoint X=302.996 Y=-79.2541 Z=0
    g121: GeomPoint X=306.073 Y=-77.8102 Z=0
    g122: LineSegment StartX=306.073 StartY=-62.8351 StartZ=0 EndX=306.073 EndY=-77.8102 EndZ=0
    g123: LineSegment StartX=302.996 StartY=-79.2541 StartZ=0 EndX=236.821 EndY=-24.2775 EndZ=0
    g124: LineSegment StartX=238.538 StartY=-21.7539 StartZ=0 EndX=302.567 EndY=-56.9099 EndZ=0
    g125: Circle CenterX=61.6457 CenterY=-88.8112 CenterZ=0 NormalX=0 NormalY=0 NormalZ=1 AngleXU=0 Radius=1
    g126: Circle CenterX=58.0728 CenterY=-91.7794 CenterZ=0 NormalX=0 NormalY=0 NormalZ=1 AngleXU=0 Radius=1
    g127: Circle CenterX=63.9135 CenterY=-91.7794 CenterZ=0 NormalX=0 NormalY=0 NormalZ=1 AngleXU=0 Radius=1
    g128: BSplineCurve PolesCount=3 KnotsCount=2 Degree=2 IsPeriodic=0
    g129: GeomPoint X=61.6457 Y=-88.8112 Z=0
    g130: GeomPoint X=63.9135 Y=-91.7794 Z=0
    g131: Circle CenterX=179.022 CenterY=-85.8163 CenterZ=0 NormalX=0 NormalY=0 NormalZ=1 AngleXU=0 Radius=1
    g132: Circle CenterX=179.022 CenterY=-91.7794 CenterZ=0 NormalX=0 NormalY=0 NormalZ=1 AngleXU=0 Radius=1
    g133: Circle CenterX=171.895 CenterY=-91.7794 CenterZ=0 NormalX=0 NormalY=0 NormalZ=1 AngleXU=0 Radius=1
    g134: BSplineCurve PolesCount=3 KnotsCount=2 Degree=2 IsPeriodic=0
    g135: GeomPoint X=179.022 Y=-85.8163 Z=0
    g136: GeomPoint X=171.895 Y=-91.7794 Z=0
    g137: Circle CenterX=185.124 CenterY=-86.2028 CenterZ=0 NormalX=0 NormalY=0 NormalZ=1 AngleXU=0 Radius=1
    g138: Circle CenterX=185.124 CenterY=-91.7794 CenterZ=0 NormalX=0 NormalY=0 NormalZ=1 AngleXU=0 Radius=1
    g139: Circle CenterX=191.747 CenterY=-91.7794 CenterZ=0 NormalX=0 NormalY=0 NormalZ=1 AngleXU=0 Radius=1
    g140: BSplineCurve PolesCount=3 KnotsCount=2 Degree=2 IsPeriodic=0
    g141: GeomPoint X=185.124 Y=-86.2028 Z=0
    g142: GeomPoint X=191.747 Y=-91.7794 Z=0
    g143: Circle CenterX=299.888 CenterY=-86.6413 CenterZ=0 NormalX=0 NormalY=0 NormalZ=1 AngleXU=0 Radius=1
    g144: Circle CenterX=306.073 CenterY=-91.7794 CenterZ=0 NormalX=0 NormalY=0 NormalZ=1 AngleXU=0 Radius=1
    g145: Circle CenterX=298.776 CenterY=-91.7794 CenterZ=0 NormalX=0 NormalY=0 NormalZ=1 AngleXU=0 Radius=1
    g146: BSplineCurve PolesCount=3 KnotsCount=2 Degree=2 IsPeriodic=0
    g147: GeomPoint X=299.888 Y=-86.6413 Z=0
    g148: GeomPoint X=298.776 Y=-91.7794 Z=0
    g149: LineSegment StartX=189.124 StartY=5.37834 StartZ=0 EndX=299.888 EndY=-86.6413 EndZ=0
    g150: LineSegment StartX=298.776 StartY=-91.7794 StartZ=0 EndX=191.747 EndY=-91.7794 EndZ=0
    g151: LineSegment StartX=185.124 StartY=-86.2028 StartZ=0 EndX=185.124 EndY=5.34704 EndZ=0
    g152: LineSegment StartX=179.022 StartY=5.34704 StartZ=0 EndX=179.022 EndY=-85.8163 EndZ=0
    g153: LineSegment StartX=171.895 StartY=-91.7794 StartZ=0 EndX=63.9135 EndY=-91.7794 EndZ=0
    g154: LineSegment StartX=61.6457 StartY=-88.8112 StartZ=0 EndX=175.022 EndY=5.37834 EndZ=0
    g155: Circle CenterX=302.073 CenterY=124.221 CenterZ=0 NormalX=0 NormalY=0 NormalZ=1 AngleXU=0 Radius=1
    g156: Circle CenterX=306.073 CenterY=124.221 CenterZ=0 NormalX=0 NormalY=0 NormalZ=1 AngleXU=0 Radius=1
    g157: Circle CenterX=302.996 CenterY=121.665 CenterZ=0 NormalX=0 NormalY=0 NormalZ=1 AngleXU=0 Radius=1
    g158: BSplineCurve PolesCount=3 KnotsCount=2 Degree=2 IsPeriodic=0
    g159: GeomPoint X=302.073 Y=124.221 Z=0
    g160: GeomPoint X=302.996 Y=121.665 Z=0
    g161: Circle CenterX=189.124 CenterY=124.221 CenterZ=0 NormalX=0 NormalY=0 NormalZ=1 AngleXU=0 Radius=1
    g162: Circle CenterX=185.124 CenterY=124.221 CenterZ=0 NormalX=0 NormalY=0 NormalZ=1 AngleXU=0 Radius=1
    g163: Circle CenterX=185.124 CenterY=120.221 CenterZ=0 NormalX=0 NormalY=0 NormalZ=1 AngleXU=0 Radius=1
    g164: BSplineCurve PolesCount=3 KnotsCount=2 Degree=2 IsPeriodic=0
    g165: GeomPoint X=189.124 Y=124.221 Z=0
    g166: GeomPoint X=185.124 Y=120.221 Z=0
    g167: Circle CenterX=175.022 CenterY=124.221 CenterZ=0 NormalX=0 NormalY=0 NormalZ=1 AngleXU=0 Radius=1
    g168: Circle CenterX=179.022 CenterY=124.221 CenterZ=0 NormalX=0 NormalY=0 NormalZ=1 AngleXU=0 Radius=1
    g169: Circle CenterX=179.022 CenterY=120.221 CenterZ=0 NormalX=0 NormalY=0 NormalZ=1 AngleXU=0 Radius=1
    g170: BSplineCurve PolesCount=3 KnotsCount=2 Degree=2 IsPeriodic=0
    g171: GeomPoint X=175.022 Y=124.221 Z=0
    g172: GeomPoint X=179.022 Y=120.221 Z=0
    g173: Circle CenterX=62.0728 CenterY=124.221 CenterZ=0 NormalX=0 NormalY=0 NormalZ=1 AngleXU=0 Radius=1
    g174: Circle CenterX=58.0728 CenterY=124.221 CenterZ=0 NormalX=0 NormalY=0 NormalZ=1 AngleXU=0 Radius=1
    g175: Circle CenterX=61.1496 CenterY=121.665 CenterZ=0 NormalX=0 NormalY=0 NormalZ=1 AngleXU=0 Radius=1
    g176: BSplineCurve PolesCount=3 KnotsCount=2 Degree=2 IsPeriodic=0
    g177: GeomPoint X=62.0728 Y=124.221 Z=0
    g178: GeomPoint X=61.1496 Y=121.665 Z=0
    g179: LineSegment StartX=179.022 StartY=120.221 StartZ=0 EndX=179.022 EndY=27.0628 EndZ=0
    g180: LineSegment StartX=185.124 StartY=27.0628 StartZ=0 EndX=185.124 EndY=120.221 EndZ=0
    g181: LineSegment StartX=302.996 StartY=121.665 StartZ=0 EndX=189.124 EndY=27.0628 EndZ=0
    g182: LineSegment StartX=175.022 StartY=27.0628 StartZ=0 EndX=61.1496 EndY=121.665 EndZ=0
    g183: Circle CenterX=61.5791 CenterY=75.4095 CenterZ=0 NormalX=0 NormalY=0 NormalZ=1 AngleXU=0 Radius=1
    g184: Circle CenterX=58.0728 CenterY=77.3346 CenterZ=0 NormalX=0 NormalY=0 NormalZ=1 AngleXU=0 Radius=1
    g185: Circle CenterX=58.0728 CenterY=73.3346 CenterZ=0 NormalX=0 NormalY=0 NormalZ=1 AngleXU=0 Radius=1
    g186: BSplineCurve PolesCount=3 KnotsCount=2 Degree=2 IsPeriodic=0
    g187: GeomPoint X=61.5791 Y=75.4095 Z=0
    g188: GeomPoint X=58.0728 Y=73.3346 Z=0
    g189: Circle CenterX=58.0728 CenterY=-40.8935 CenterZ=0 NormalX=0 NormalY=0 NormalZ=1 AngleXU=0 Radius=1
    g190: Circle CenterX=58.0728 CenterY=-44.8935 CenterZ=0 NormalX=0 NormalY=0 NormalZ=1 AngleXU=0 Radius=1
    g191: Circle CenterX=61.5791 CenterY=-42.9683 CenterZ=0 NormalX=0 NormalY=0 NormalZ=1 AngleXU=0 Radius=1
    g192: BSplineCurve PolesCount=3 KnotsCount=2 Degree=2 IsPeriodic=0
    g193: GeomPoint X=58.0728 Y=-40.8935 Z=0
    g194: GeomPoint X=61.5791 Y=-42.9683 Z=0
    g195: LineSegment StartX=61.5791 StartY=-42.9683 StartZ=0 EndX=165.871 EndY=14.2954 EndZ=0
    g196: LineSegment StartX=165.871 StartY=18.1458 StartZ=0 EndX=61.5791 EndY=75.4095 EndZ=0
    g197: LineSegment StartX=58.0728 StartY=73.3346 StartZ=0 EndX=58.0728 EndY=-40.8935 EndZ=0
    g198: Circle CenterX=302.567 CenterY=-42.9683 CenterZ=0 NormalX=0 NormalY=0 NormalZ=1 AngleXU=0 Radius=1
    g199: Circle CenterX=306.073 CenterY=-44.8935 CenterZ=0 NormalX=0 NormalY=0 NormalZ=1 AngleXU=0 Radius=1
    g200: Circle CenterX=306.073 CenterY=-40.8935 CenterZ=0 NormalX=0 NormalY=0 NormalZ=1 AngleXU=0 Radius=1
    g201: BSplineCurve PolesCount=3 KnotsCount=2 Degree=2 IsPeriodic=0
    g202: GeomPoint X=302.567 Y=-42.9683 Z=0
    g203: GeomPoint X=306.073 Y=-40.8935 Z=0
    g204: Circle CenterX=306.073 CenterY=73.3346 CenterZ=0 NormalX=0 NormalY=0 NormalZ=1 AngleXU=0 Radius=1
    g205: Circle CenterX=306.073 CenterY=77.3346 CenterZ=0 NormalX=0 NormalY=0 NormalZ=1 AngleXU=0 Radius=1
    g206: Circle CenterX=302.567 CenterY=75.4095 CenterZ=0 NormalX=0 NormalY=0 NormalZ=1 AngleXU=0 Radius=1
    g207: BSplineCurve PolesCount=3 KnotsCount=2 Degree=2 IsPeriodic=0
    g208: GeomPoint X=306.073 Y=73.3346 Z=0
    g209: GeomPoint X=302.567 Y=75.4095 Z=0
    g210: LineSegment StartX=302.567 StartY=-42.9683 StartZ=0 EndX=198.275 EndY=14.2954 EndZ=0
    g211: LineSegment StartX=198.275 StartY=18.1458 StartZ=0 EndX=302.567 EndY=75.4095 EndZ=0
    g212: LineSegment StartX=306.073 StartY=73.3346 StartZ=0 EndX=306.073 EndY=-40.8935 EndZ=0
    g213: LineSegment StartX=322.073 StartY=105.865 StartZ=0 EndX=328.643 EndY=105.865 EndZ=0
    g214: LineSegment StartX=318.073 StartY=120.221 StartZ=0 EndX=318.073 EndY=109.865 EndZ=0
    g215: LineSegment StartX=336.157 StartY=107.779 StartZ=0 EndX=362.567 EndY=122.294 EndZ=0
    g216: Circle CenterX=362.073 CenterY=124.221 CenterZ=0 NormalX=0 NormalY=0 NormalZ=1 AngleXU=0 Radius=1
    g217: Circle CenterX=366.073 CenterY=124.221 CenterZ=0 NormalX=0 NormalY=0 NormalZ=1 AngleXU=0 Radius=1
    g218: Circle CenterX=362.567 CenterY=122.294 CenterZ=0 NormalX=0 NormalY=0 NormalZ=1 AngleXU=0 Radius=1
    g219: BSplineCurve PolesCount=3 KnotsCount=2 Degree=2 IsPeriodic=0
    g220: GeomPoint X=362.073 Y=124.221 Z=0
    g221: GeomPoint X=362.567 Y=122.294 Z=0
    g222: Circle CenterX=322.073 CenterY=124.221 CenterZ=0 NormalX=0 NormalY=0 NormalZ=1 AngleXU=0 Radius=1
    g223: Circle CenterX=318.073 CenterY=124.221 CenterZ=0 NormalX=0 NormalY=0 NormalZ=1 AngleXU=0 Radius=1
    g224: Circle CenterX=318.073 CenterY=120.221 CenterZ=0 NormalX=0 NormalY=0 NormalZ=1 AngleXU=0 Radius=1
    g225: BSplineCurve PolesCount=3 KnotsCount=2 Degree=2 IsPeriodic=0
    g226: GeomPoint X=322.073 Y=124.221 Z=0
    g227: GeomPoint X=318.073 Y=120.221 Z=0
    g228: Circle CenterX=322.073 CenterY=105.865 CenterZ=0 NormalX=0 NormalY=0 NormalZ=1 AngleXU=0 Radius=1
    g229: Circle CenterX=318.073 CenterY=105.865 CenterZ=0 NormalX=0 NormalY=0 NormalZ=1 AngleXU=0 Radius=1
    g230: Circle CenterX=318.073 CenterY=109.865 CenterZ=0 NormalX=0 NormalY=0 NormalZ=1 AngleXU=0 Radius=1
    g231: BSplineCurve PolesCount=3 KnotsCount=2 Degree=2 IsPeriodic=0
    g232: GeomPoint X=322.073 Y=105.865 Z=0
    g233: GeomPoint X=318.073 Y=109.865 Z=0
    g234: Circle CenterX=336.157 CenterY=107.779 CenterZ=0 NormalX=0 NormalY=0 NormalZ=1 AngleXU=0 Radius=1
    g235: Circle CenterX=332.651 CenterY=105.853 CenterZ=0 NormalX=0 NormalY=0 NormalZ=1 AngleXU=0 Radius=1
    g236: Circle CenterX=328.643 CenterY=105.865 CenterZ=0 NormalX=0 NormalY=0 NormalZ=1 AngleXU=0 Radius=1
    g237: BSplineCurve PolesCount=3 KnotsCount=2 Degree=2 IsPeriodic=0
    g238: GeomPoint X=336.157 Y=107.779 Z=0
    g239: GeomPoint X=328.643 Y=105.865 Z=0
    g240: LineSegment StartX=322.073 StartY=124.221 StartZ=0 EndX=362.073 EndY=124.221 EndZ=0
    g241: Circle CenterX=371.567 CenterY=-80.8644 CenterZ=0 NormalX=0 NormalY=0 NormalZ=1 AngleXU=0 Radius=1
    g242: Circle CenterX=375.073 CenterY=-82.7896 CenterZ=0 NormalX=0 NormalY=0 NormalZ=1 AngleXU=0 Radius=1
    g243: Circle CenterX=375.073 CenterY=-78.7896 CenterZ=0 NormalX=0 NormalY=0 NormalZ=1 AngleXU=0 Radius=1
    g244: BSplineCurve PolesCount=3 KnotsCount=2 Degree=2 IsPeriodic=0
    g245: GeomPoint X=371.567 Y=-80.8644 Z=0
    g246: GeomPoint X=375.073 Y=-78.7896 Z=0
    g247: Circle CenterX=321.579 CenterY=-53.4075 CenterZ=0 NormalX=0 NormalY=0 NormalZ=1 AngleXU=0 Radius=1
    g248: Circle CenterX=318.073 CenterY=-51.4823 CenterZ=0 NormalX=0 NormalY=0 NormalZ=1 AngleXU=0 Radius=1
    g249: Circle CenterX=318.073 CenterY=-47.4805 CenterZ=0 NormalX=0 NormalY=0 NormalZ=1 AngleXU=0 Radius=1
    g250: BSplineCurve PolesCount=3 KnotsCount=2 Degree=2 IsPeriodic=0
    g251: GeomPoint X=321.579 Y=-53.4075 Z=0
    g252: GeomPoint X=318.073 Y=-47.4805 Z=0
    g253: LineSegment StartX=371.567 StartY=-80.8644 StartZ=0 EndX=321.579 EndY=-53.4075 EndZ=0
    g254: Circle CenterX=321.579 CenterY=-67.3492 CenterZ=0 NormalX=0 NormalY=0 NormalZ=1 AngleXU=0 Radius=1
    g255: Circle CenterX=318.073 CenterY=-65.424 CenterZ=0 NormalX=0 NormalY=0 NormalZ=1 AngleXU=0 Radius=1
    g256: Circle CenterX=318.073 CenterY=-69.424 CenterZ=0 NormalX=0 NormalY=0 NormalZ=1 AngleXU=0 Radius=1
    g257: BSplineCurve PolesCount=3 KnotsCount=2 Degree=2 IsPeriodic=0
    g258: GeomPoint X=321.579 Y=-67.3492 Z=0
    g259: GeomPoint X=318.073 Y=-69.424 Z=0
    g260: Circle CenterX=362.567 CenterY=-89.8542 CenterZ=0 NormalX=0 NormalY=0 NormalZ=1 AngleXU=0 Radius=1
    g261: Circle CenterX=366.073 CenterY=-91.7794 CenterZ=0 NormalX=0 NormalY=0 NormalZ=1 AngleXU=0 Radius=1
    g262: Circle CenterX=362.073 CenterY=-91.7794 CenterZ=0 NormalX=0 NormalY=0 NormalZ=1 AngleXU=0 Radius=1
    g263: BSplineCurve PolesCount=3 KnotsCount=2 Degree=2 IsPeriodic=0
    g264: GeomPoint X=362.567 Y=-89.8542 Z=0
    g265: GeomPoint X=362.073 Y=-91.7794 Z=0
    g266: Circle CenterX=322.073 CenterY=-91.7794 CenterZ=0 NormalX=0 NormalY=0 NormalZ=1 AngleXU=0 Radius=1
    g267: Circle CenterX=318.073 CenterY=-91.7794 CenterZ=0 NormalX=0 NormalY=0 NormalZ=1 AngleXU=0 Radius=1
    g268: Circle CenterX=318.073 CenterY=-87.7794 CenterZ=0 NormalX=0 NormalY=0 NormalZ=1 AngleXU=0 Radius=1
    g269: BSplineCurve PolesCount=3 KnotsCount=2 Degree=2 IsPeriodic=0
    g270: GeomPoint X=322.073 Y=-91.7794 Z=0
    g271: GeomPoint X=318.073 Y=-87.7794 Z=0
    g272: LineSegment StartX=362.567 StartY=-89.8542 StartZ=0 EndX=321.579 EndY=-67.3492 EndZ=0
    g273: LineSegment StartX=318.073 StartY=-69.424 StartZ=0 EndX=318.073 EndY=-87.7794 EndZ=0
    g274: LineSegment StartX=322.073 StartY=-91.7794 StartZ=0 EndX=362.073 EndY=-91.7794 EndZ=0
    g275: Circle CenterX=2.07281 CenterY=124.221 CenterZ=0 NormalX=0 NormalY=0 NormalZ=1 AngleXU=0 Radius=1
    g276: Circle CenterX=1.57905 CenterY=122.295 CenterZ=0 NormalX=0 NormalY=0 NormalZ=1 AngleXU=0 Radius=1
    g277: BSplineCurve PolesCount=3 KnotsCount=2 Degree=2 IsPeriodic=0
    g278: GeomPoint X=2.07281 Y=124.221 Z=0
    g279: GeomPoint X=1.57905 Y=122.295 Z=0
    g280: Circle CenterX=42.0728 CenterY=124.221 CenterZ=0 NormalX=0 NormalY=0 NormalZ=1 AngleXU=0 Radius=1
    g281: Circle CenterX=46.0728 CenterY=124.221 CenterZ=0 NormalX=0 NormalY=0 NormalZ=1 AngleXU=0 Radius=1
    g282: Circle CenterX=46.0728 CenterY=120.221 CenterZ=0 NormalX=0 NormalY=0 NormalZ=1 AngleXU=0 Radius=1
    g283: BSplineCurve PolesCount=3 KnotsCount=2 Degree=2 IsPeriodic=0
    g284: GeomPoint X=42.0728 Y=124.221 Z=0
    g285: GeomPoint X=46.0728 Y=120.221 Z=0
    g286: Circle CenterX=46.0728 CenterY=109.865 CenterZ=0 NormalX=0 NormalY=0 NormalZ=1 AngleXU=0 Radius=1
    g287: Circle CenterX=46.0728 CenterY=105.865 CenterZ=0 NormalX=0 NormalY=0 NormalZ=1 AngleXU=0 Radius=1
    g288: Circle CenterX=42.0728 CenterY=105.865 CenterZ=0 NormalX=0 NormalY=0 NormalZ=1 AngleXU=0 Radius=1
    g289: BSplineCurve PolesCount=3 KnotsCount=2 Degree=2 IsPeriodic=0
    g290: GeomPoint X=46.0728 Y=109.865 Z=0
    g291: GeomPoint X=42.0728 Y=105.865 Z=0
    g292: Circle CenterX=35.5028 CenterY=105.865 CenterZ=0 NormalX=0 NormalY=0 NormalZ=1 AngleXU=0 Radius=1
    g293: Circle CenterX=31.5028 CenterY=105.865 CenterZ=0 NormalX=0 NormalY=0 NormalZ=1 AngleXU=0 Radius=1
    g294: Circle CenterX=27.9965 CenterY=107.79 CenterZ=0 NormalX=0 NormalY=0 NormalZ=1 AngleXU=0 Radius=1
    g295: BSplineCurve PolesCount=3 KnotsCount=2 Degree=2 IsPeriodic=0
    g296: GeomPoint X=35.5028 Y=105.865 Z=0
    g297: GeomPoint X=27.9965 Y=107.79 Z=0
    g298: LineSegment StartX=2.07281 StartY=124.221 StartZ=0 EndX=42.0728 EndY=124.221 EndZ=0
    g299: LineSegment StartX=46.0728 StartY=120.221 StartZ=0 EndX=46.0728 EndY=109.865 EndZ=0
    g300: LineSegment StartX=42.0728 StartY=105.865 StartZ=0 EndX=35.5028 EndY=105.865 EndZ=0
    g301: LineSegment StartX=27.9965 StartY=107.79 StartZ=0 EndX=1.57905 EndY=122.295 EndZ=0
    g302: Circle CenterX=42.5666 CenterY=-67.3492 CenterZ=0 NormalX=0 NormalY=0 NormalZ=1 AngleXU=0 Radius=1
    g303: Circle CenterX=46.0728 CenterY=-65.424 CenterZ=0 NormalX=0 NormalY=0 NormalZ=1 AngleXU=0 Radius=1
    g304: Circle CenterX=46.0728 CenterY=-69.424 CenterZ=0 NormalX=0 NormalY=0 NormalZ=1 AngleXU=0 Radius=1
    g305: BSplineCurve PolesCount=3 KnotsCount=2 Degree=2 IsPeriodic=0
    g306: GeomPoint X=42.5666 Y=-67.3492 Z=0
    g307: GeomPoint X=46.0728 Y=-69.424 Z=0
    g308: Circle CenterX=46.0728 CenterY=-87.7794 CenterZ=0 NormalX=0 NormalY=0 NormalZ=1 AngleXU=0 Radius=1
    g309: Circle CenterX=46.0728 CenterY=-91.7794 CenterZ=0 NormalX=0 NormalY=0 NormalZ=1 AngleXU=0 Radius=1
    g310: Circle CenterX=42.0728 CenterY=-91.7794 CenterZ=0 NormalX=0 NormalY=0 NormalZ=1 AngleXU=0 Radius=1
    g311: BSplineCurve PolesCount=3 KnotsCount=2 Degree=2 IsPeriodic=0
    g312: GeomPoint X=46.0728 Y=-87.7794 Z=0
    g313: GeomPoint X=42.0728 Y=-91.7794 Z=0
    g314: Circle CenterX=2.07281 CenterY=-91.7794 CenterZ=0 NormalX=0 NormalY=0 NormalZ=1 AngleXU=0 Radius=1
    g315: Circle CenterX=-1.92719 CenterY=-91.7794 CenterZ=0 NormalX=0 NormalY=0 NormalZ=1 AngleXU=0 Radius=1
    g316: Circle CenterX=1.57905 CenterY=-89.8542 CenterZ=0 NormalX=0 NormalY=0 NormalZ=1 AngleXU=0 Radius=1
    g317: BSplineCurve PolesCount=3 KnotsCount=2 Degree=2 IsPeriodic=0
    g318: GeomPoint X=2.07281 Y=-91.7794 Z=0
    g319: GeomPoint X=1.57905 Y=-89.8542 Z=0
    g320: LineSegment StartX=2.07281 StartY=-91.7794 StartZ=0 EndX=42.0728 EndY=-91.7794 EndZ=0
    g321: LineSegment StartX=46.0728 StartY=-87.7794 StartZ=0 EndX=46.0728 EndY=-69.424 EndZ=0
    g322: LineSegment StartX=42.5666 StartY=-67.3492 StartZ=0 EndX=1.57905 EndY=-89.8542 EndZ=0
    g323: Circle CenterX=322.073 CenterY=76.4095 CenterZ=0 NormalX=0 NormalY=0 NormalZ=1 AngleXU=0 Radius=4
    g324: BSplineCurve PolesCount=3 KnotsCount=2 Degree=2 IsPeriodic=0
    g325: GeomPoint X=318.073 Y=72.4095 Z=0
    g326: GeomPoint X=322.073 Y=76.4095 Z=0
    g327: Circle CenterX=375.073 CenterY=72.4095 CenterZ=0 NormalX=0 NormalY=0 NormalZ=1 AngleXU=0 Radius=1
    g328: Circle CenterX=375.073 CenterY=76.4095 CenterZ=0 NormalX=0 NormalY=0 NormalZ=1 AngleXU=0 Radius=1
    g329: Circle CenterX=371.073 CenterY=76.4095 CenterZ=0 NormalX=0 NormalY=0 NormalZ=1 AngleXU=0 Radius=1
    g330: BSplineCurve PolesCount=3 KnotsCount=2 Degree=2 IsPeriodic=0
    g331: GeomPoint X=375.073 Y=72.4095 Z=0
    g332: GeomPoint X=371.073 Y=76.4095 Z=0
    g333: LineSegment StartX=322.073 StartY=76.4095 StartZ=0 EndX=371.073 EndY=76.4095 EndZ=0
    g334: LineSegment StartX=318.073 StartY=72.4095 StartZ=0 EndX=318.073 EndY=-47.4805 EndZ=0
    g335: LineSegment StartX=375.073 StartY=72.4095 StartZ=0 EndX=375.073 EndY=-78.7896 EndZ=0
    g336: ArcOfCircle CenterX=-26.9272 CenterY=22.1087 CenterZ=0 NormalX=0 NormalY=0 NormalZ=1 AngleXU=0 Radius=4 StartAngle=5e-16 EndAngle=3.14159
    g337: LineSegment StartX=-22.9272 StartY=22.1087 StartZ=0 EndX=-18.9272 EndY=-83.7794 EndZ=0
    g338: LineSegment StartX=-34.9272 StartY=-83.7794 StartZ=0 EndX=-30.9272 EndY=22.1087 EndZ=0
    g339: ArcOfCircle CenterX=391.073 CenterY=22.1087 CenterZ=0 NormalX=0 NormalY=0 NormalZ=1 AngleXU=0 Radius=4 StartAngle=0 EndAngle=3.14159
    g340: LineSegment StartX=387.073 StartY=22.1087 StartZ=0 EndX=383.073 EndY=-83.7794 EndZ=0
    g341: LineSegment StartX=395.073 StartY=22.1087 StartZ=0 EndX=399.073 EndY=-83.7794 EndZ=0
    g342: Circle CenterX=-10.9272 CenterY=-78.7794 CenterZ=0 NormalX=0 NormalY=0 NormalZ=1 AngleXU=0 Radius=1
    g343: Circle CenterX=-10.9272 CenterY=-82.7794 CenterZ=0 NormalX=0 NormalY=0 NormalZ=1 AngleXU=0 Radius=1
    g344: Circle CenterX=-7.42095 CenterY=-80.8542 CenterZ=0 NormalX=0 NormalY=0 NormalZ=1 AngleXU=0 Radius=1
    g345: BSplineCurve PolesCount=3 KnotsCount=2 Degree=2 IsPeriodic=0
    g346: GeomPoint X=-10.9272 Y=-78.7794 Z=0
    g347: GeomPoint X=-7.42095 Y=-80.8542 Z=0
    g348: Circle CenterX=42.5666 CenterY=-53.4075 CenterZ=0 NormalX=0 NormalY=0 NormalZ=1 AngleXU=0 Radius=1
    g349: Circle CenterX=46.0728 CenterY=-51.4823 CenterZ=0 NormalX=0 NormalY=0 NormalZ=1 AngleXU=0 Radius=1
    g350: Circle CenterX=46.0728 CenterY=-47.4823 CenterZ=0 NormalX=0 NormalY=0 NormalZ=1 AngleXU=0 Radius=1
    g351: BSplineCurve PolesCount=3 KnotsCount=2 Degree=2 IsPeriodic=0
    g352: GeomPoint X=42.5666 Y=-53.4075 Z=0
    g353: GeomPoint X=46.0728 Y=-47.4823 Z=0
    g354: Circle CenterX=46.0728 CenterY=72.4095 CenterZ=0 NormalX=0 NormalY=0 NormalZ=1 AngleXU=0 Radius=1
    g355: Circle CenterX=46.0728 CenterY=76.4095 CenterZ=0 NormalX=0 NormalY=0 NormalZ=1 AngleXU=0 Radius=1
    g356: Circle CenterX=42.0728 CenterY=76.4095 CenterZ=0 NormalX=0 NormalY=0 NormalZ=1 AngleXU=0 Radius=1
    g357: BSplineCurve PolesCount=3 KnotsCount=2 Degree=2 IsPeriodic=0
    g358: GeomPoint X=46.0728 Y=72.4095 Z=0
    g359: GeomPoint X=42.0728 Y=76.4095 Z=0
    g360: Circle CenterX=-6.92718 CenterY=76.4095 CenterZ=0 NormalX=0 NormalY=0 NormalZ=1 AngleXU=0 Radius=1
    g361: Circle CenterX=-10.9272 CenterY=76.4095 CenterZ=0 NormalX=0 NormalY=0 NormalZ=1 AngleXU=0 Radius=1
    g362: Circle CenterX=-10.9272 CenterY=72.4095 CenterZ=0 NormalX=0 NormalY=0 NormalZ=1 AngleXU=0 Radius=1
    g363: BSplineCurve PolesCount=3 KnotsCount=2 Degree=2 IsPeriodic=0
    g364: GeomPoint X=-6.92718 Y=76.4095 Z=0
    g365: GeomPoint X=-10.9272 Y=72.4095 Z=0
    g366: LineSegment StartX=-10.9272 StartY=72.4095 StartZ=0 EndX=-10.9272 EndY=-78.7794 EndZ=0
    g367: LineSegment StartX=-7.42095 StartY=-80.8542 StartZ=0 EndX=42.5666 EndY=-53.4075 EndZ=0
    g368: LineSegment StartX=46.0728 StartY=-47.4823 StartZ=0 EndX=46.0728 EndY=72.4095 EndZ=0
    g369: LineSegment StartX=42.0728 StartY=76.4095 StartZ=0 EndX=-6.92719 EndY=76.4095 EndZ=0
    g370: LineSegment StartX=232.072 StartY=136.221 StartZ=0 EndX=232.072 EndY=-117.815 EndZ=0
    g371: LineSegment StartX=132.072 StartY=136.221 StartZ=0 EndX=132.072 EndY=-121.309 EndZ=0
    g372: LineSegment StartX=245.072 StartY=136.221 StartZ=0 EndX=245.072 EndY=-116.499 EndZ=0
    g373: LineSegment StartX=119.072 StartY=136.221 StartZ=0 EndX=119.072 EndY=-116.228 EndZ=0
    g374: LineSegment StartX=-42.9272 StartY=136.221 StartZ=0 EndX=407.073 EndY=136.221 EndZ=0
    g375: LineSegment StartX=232.072 StartY=136.221 StartZ=0 EndX=220.072 EndY=136.221 EndZ=0
    g376: LineSegment StartX=232.072 StartY=136.221 StartZ=0 EndX=232.072 EndY=124.221 EndZ=0
    g377: LineSegment StartX=220.072 StartY=136.221 StartZ=0 EndX=220.072 EndY=124.221 EndZ=0
    g378: LineSegment StartX=220.072 StartY=136.221 StartZ=0 EndX=226.072 EndY=136.221 EndZ=0
    g379: LineSegment StartX=220.072 StartY=136.221 StartZ=0 EndX=220.072 EndY=130.221 EndZ=0
    g380: LineSegment StartX=220.072 StartY=124.221 StartZ=0 EndX=226.072 EndY=124.221 EndZ=0
    g381: LineSegment StartX=232.072 StartY=124.221 StartZ=0 EndX=232.072 EndY=127.221 EndZ=0
    g382: LineSegment StartX=232.072 StartY=136.221 StartZ=0 EndX=232.072 EndY=133.221 EndZ=0
    g383-g387: Circle x5 (B-spline internal-alignment scaffolding for g388; pole/knot coordinates omitted)
    g388: BSplineCurve PolesCount=5 KnotsCount=3 Degree=3 IsPeriodic=0
    g389: GeomPoint X=232.072 Y=133.221 Z=0
    g390: GeomPoint X=223.072 Y=130.221 Z=0
    g391: GeomPoint X=232.072 Y=127.221 Z=0
    g392: LineSegment StartX=189.124 StartY=124.221 StartZ=0 EndX=302.073 EndY=124.221 EndZ=0
    g393: LineSegment StartX=132.072 StartY=136.221 StartZ=0 EndX=132.072 EndY=124.221 EndZ=0
    g394: LineSegment StartX=132.072 StartY=136.221 StartZ=0 EndX=144.072 EndY=136.221 EndZ=0
    g395: LineSegment StartX=144.072 StartY=136.221 StartZ=0 EndX=144.072 EndY=124.221 EndZ=0
    g396: LineSegment StartX=144.072 StartY=124.221 StartZ=0 EndX=138.072 EndY=124.221 EndZ=0
    g397: LineSegment StartX=144.596 StartY=138.519 StartZ=0 EndX=138.596 EndY=138.519 EndZ=0
  constraints (672):
    c: Vertical(g0)
    c: Vertical(g1)
    c: Block(g1)
    c: Block(g0)
    c: Weight(g4) = 1
    c: Equal(g4,g5)
    c: Equal(g4,g6)
    c: InternalAlignment(g4,g7)
    c: InternalAlignment(g5,g7)
    c: InternalAlignment(g6,g7)
    c: InternalAlignment(g8,g7)
    c: InternalAlignment(g9,g7)
    c: Weight(g10) = 1
    c: Equal(g10,g11)
    c: Equal(g10,g12)
    c: InternalAlignment(g10,g13)
    c: InternalAlignment(g11,g13)
    c: InternalAlignment(g12,g13)
    c: InternalAlignment(g14,g13)
    c: InternalAlignment(g15,g13)
    c: Block(g13)
    c: Block(g7)
    c: Weight(g16) = 1
    c: Equal(g16,g17)
    c: Equal(g16,g18)
    c: InternalAlignment(g16,g19)
    c: InternalAlignment(g17,g19)
    c: InternalAlignment(g18,g19)
    c: InternalAlignment(g20,g19)
    c: InternalAlignment(g21,g19)
    c: Weight(g22) = 1
    c: Equal(g22,g23)
    c: Equal(g22,g24)
    c: InternalAlignment(g22,g25)
    c: InternalAlignment(g23,g25)
    c: InternalAlignment(g24,g25)
    c: InternalAlignment(g26,g25)
    c: InternalAlignment(g27,g25)
    c: Block(g25)
    c: Block(g19)
    c: Weight(g28) = 1
    c: Equal(g28,g29)
    c: Equal(g28,g30)
    c: InternalAlignment(g28,g31)
    c: InternalAlignment(g29,g31)
    c: InternalAlignment(g30,g31)
    c: InternalAlignment(g32,g31)
    c: InternalAlignment(g33,g31)
    c: Weight(g34) = 1
    c: Equal(g34,g35)
    c: Equal(g34,g36)
    c: InternalAlignment(g34,g37)
    c: InternalAlignment(g35,g37)
    c: InternalAlignment(g36,g37)
    c: InternalAlignment(g38,g37)
    c: InternalAlignment(g39,g37)
    c: Block(g31)
    c: Block(g37)
    c: Coincident(g40,g1)
    c: Coincident(g40,g0)
    c: Horizontal(g40)
    c: Distance(g40) = 450
    c: Weight(g41) = 1
    c: Equal(g41,g42)
    c: Equal(g41,g43)
    c: InternalAlignment(g41,g44)
    c: InternalAlignment(g42,g44)
    c: InternalAlignment(g43,g44)
    c: InternalAlignment(g45,g44)
    c: InternalAlignment(g46,g44)
    c: Block(g44)
    c: Weight(g47) = 1
    c: Equal(g47,g48)
    c: Equal(g47,g49)
    c: InternalAlignment(g47,g50)
    c: InternalAlignment(g48,g50)
    c: InternalAlignment(g49,g50)
    c: InternalAlignment(g51,g50)
    c: InternalAlignment(g52,g50)
    c: Block(g50)
    c: Weight(g53) = 1
    c: Equal(g53,g54)
    c: Equal(g53,g55)
    c: InternalAlignment(g53,g56)
    c: InternalAlignment(g54,g56)
    c: InternalAlignment(g55,g56)
    c: InternalAlignment(g57,g56)
    c: InternalAlignment(g58,g56)
    c: Block(g56)
    c: Weight(g59) = 1
    c: Equal(g59,g60)
    c: Equal(g59,g61)
    c: InternalAlignment(g59,g62)
    c: InternalAlignment(g60,g62)
    c: InternalAlignment(g61,g62)
    c: InternalAlignment(g63,g62)
    c: InternalAlignment(g64,g62)
    c: Block(g62)
    c: Weight(g65) = 1
    c: Equal(g65,g66)
    c: Equal(g65,g67)
    c: InternalAlignment(g65,g68)
    c: InternalAlignment(g66,g68)
    c: InternalAlignment(g67,g68)
    c: InternalAlignment(g69,g68)
    c: InternalAlignment(g70,g68)
    c: Weight(g71) = 1
    c: Equal(g71,g72)
    c: Equal(g71,g73)
    c: InternalAlignment(g71,g74)
    c: InternalAlignment(g72,g74)
    c: InternalAlignment(g73,g74)
    c: InternalAlignment(g75,g74)
    c: InternalAlignment(g76,g74)
    c: Block(g68)
    c: Block(g74)
    c: Coincident(g77,g68)
    c: Coincident(g77,g74)
    c: Vertical(g77)
    c: Coincident(g78,g68)
    c: Coincident(g78,g50)
    c: Coincident(g79,g50)
    c: Coincident(g79,g74)
    c: Weight(g80) = 1
    c: Equal(g80,g81)
    c: Equal(g80,g82)
    c: InternalAlignment(g80,g83)
    c: InternalAlignment(g81,g83)
    c: InternalAlignment(g82,g83)
    c: InternalAlignment(g84,g83)
    c: InternalAlignment(g85,g83)
    c: Weight(g86) = 1
    c: Equal(g86,g87)
    c: Equal(g86,g88)
    c: InternalAlignment(g86,g89)
    c: InternalAlignment(g87,g89)
    c: InternalAlignment(g88,g89)
    c: InternalAlignment(g90,g89)
    c: InternalAlignment(g91,g89)
    c: Block(g83)
    c: Block(g89)
    c: Coincident(g92,g83)
    c: Coincident(g92,g89)
    c: Vertical(g92)
    c: Coincident(g93,g83)
    c: Coincident(g93,g44)
    c: Coincident(g94,g44)
    c: Coincident(g94,g89)
    c: Weight(g95) = 1
    c: Equal(g95,g96)
    c: Equal(g95,g97)
    c: InternalAlignment(g95,g98)
    c: InternalAlignment(g96,g98)
    c: InternalAlignment(g97,g98)
    c: InternalAlignment(g99,g98)
    c: InternalAlignment(g100,g98)
    c: Weight(g101) = 1
    c: Equal(g101,g102)
    c: Equal(g101,g103)
    c: InternalAlignment(g101,g104)
    c: InternalAlignment(g102,g104)
    c: InternalAlignment(g103,g104)
    c: InternalAlignment(g105,g104)
    c: InternalAlignment(g106,g104)
    c: Block(g98)
    c: Block(g104)
    c: Coincident(g107,g98)
    c: Coincident(g107,g104)
    c: Vertical(g107)
    c: Coincident(g108,g104)
    c: Coincident(g108,g62)
    c: Coincident(g109,g62)
    c: Coincident(g109,g98)
    c: Weight(g110) = 1
    c: Equal(g110,g111)
    c: Equal(g110,g112)
    c: InternalAlignment(g110,g113)
    c: InternalAlignment(g111,g113)
    c: InternalAlignment(g112,g113)
    c: InternalAlignment(g114,g113)
    c: InternalAlignment(g115,g113)
    c: Weight(g116) = 1
    c: Equal(g116,g117)
    c: Equal(g116,g118)
    c: InternalAlignment(g116,g119)
    c: InternalAlignment(g117,g119)
    c: InternalAlignment(g118,g119)
    c: InternalAlignment(g120,g119)
    c: InternalAlignment(g121,g119)
    c: Block(g113)
    c: Block(g119)
    c: Coincident(g122,g113)
    c: Coincident(g122,g119)
    c: Vertical(g122)
    c: Coincident(g123,g119)
    c: Coincident(g123,g56)
    c: Coincident(g124,g56)
    c: Coincident(g124,g113)
    c: Weight(g125) = 1
    c: Equal(g125,g126)
    c: Equal(g125,g127)
    c: InternalAlignment(g125,g128)
    c: InternalAlignment(g126,g128)
    c: InternalAlignment(g127,g128)
    c: InternalAlignment(g129,g128)
    c: InternalAlignment(g130,g128)
    c: Weight(g131) = 1
    c: Equal(g131,g132)
    c: Equal(g131,g133)
    c: InternalAlignment(g131,g134)
    c: InternalAlignment(g132,g134)
    c: InternalAlignment(g133,g134)
    c: InternalAlignment(g135,g134)
    c: InternalAlignment(g136,g134)
    c: Weight(g137) = 1
    c: Equal(g137,g138)
    c: Equal(g137,g139)
    c: InternalAlignment(g137,g140)
    c: InternalAlignment(g138,g140)
    c: InternalAlignment(g139,g140)
    c: InternalAlignment(g141,g140)
    c: InternalAlignment(g142,g140)
    c: Weight(g143) = 1
    c: Equal(g143,g144)
    c: Equal(g143,g145)
    c: InternalAlignment(g143,g146)
    c: InternalAlignment(g144,g146)
    c: InternalAlignment(g145,g146)
    c: InternalAlignment(g147,g146)
    c: InternalAlignment(g148,g146)
    c: Block(g146)
    c: Block(g140)
    c: Block(g134)
    c: Block(g128)
    c: Coincident(g149,g25)
    c: Coincident(g149,g146)
    c: Coincident(g150,g146)
    c: Coincident(g150,g140)
    c: Horizontal(g150)
    c: Coincident(g151,g140)
    c: Coincident(g151,g25)
    c: Vertical(g151)
    c: Coincident(g152,g19)
    c: Coincident(g152,g134)
    c: Vertical(g152)
    c: Coincident(g153,g134)
    c: Coincident(g153,g128)
    c: Horizontal(g153)
    c: Coincident(g154,g128)
    c: Coincident(g154,g19)
    c: Weight(g155) = 1
    c: Equal(g155,g156)
    c: Equal(g155,g157)
    c: InternalAlignment(g155,g158)
    c: InternalAlignment(g156,g158)
    c: InternalAlignment(g157,g158)
    c: InternalAlignment(g159,g158)
    c: InternalAlignment(g160,g158)
    c: Weight(g161) = 1
    c: Equal(g161,g162)
    c: Equal(g161,g163)
    c: InternalAlignment(g161,g164)
    c: InternalAlignment(g162,g164)
    c: InternalAlignment(g163,g164)
    c: InternalAlignment(g165,g164)
    c: InternalAlignment(g166,g164)
    c: Weight(g167) = 1
    c: Equal(g167,g168)
    c: Equal(g167,g169)
    c: InternalAlignment(g167,g170)
    c: InternalAlignment(g168,g170)
    c: InternalAlignment(g169,g170)
    c: InternalAlignment(g171,g170)
    c: InternalAlignment(g172,g170)
    c: Weight(g173) = 1
    c: Equal(g173,g174)
    c: Equal(g173,g175)
    c: InternalAlignment(g173,g176)
    c: InternalAlignment(g174,g176)
    c: InternalAlignment(g175,g176)
    c: InternalAlignment(g177,g176)
    c: InternalAlignment(g178,g176)
    c: Block(g176)
    c: Block(g170)
    c: Block(g164)
    c: Block(g158)
    c: Coincident(g179,g170)
    c: Coincident(g179,g7)
    c: Vertical(g179)
    c: Coincident(g180,g13)
    c: Coincident(g180,g164)
    c: Vertical(g180)
    c: Coincident(g181,g158)
    c: Coincident(g181,g13)
    c: Coincident(g182,g7)
    c: Weight(g183) = 1
    c: Equal(g183,g184)
    c: Equal(g183,g185)
    c: InternalAlignment(g183,g186)
    c: InternalAlignment(g184,g186)
    c: InternalAlignment(g185,g186)
    c: InternalAlignment(g187,g186)
    c: InternalAlignment(g188,g186)
    c: Weight(g189) = 1
    c: Equal(g189,g190)
    c: Equal(g189,g191)
    c: InternalAlignment(g189,g192)
    c: InternalAlignment(g190,g192)
    c: InternalAlignment(g191,g192)
    c: InternalAlignment(g193,g192)
    c: InternalAlignment(g194,g192)
    c: Block(g192)
    c: Block(g186)
    c: Coincident(g195,g192)
    c: Coincident(g195,g31)
    c: Coincident(g196,g31)
    c: Coincident(g196,g186)
    c: Coincident(g197,g186)
    c: Coincident(g197,g192)
    c: Vertical(g197)
    c: Weight(g198) = 1
    c: Equal(g198,g199)
    c: Equal(g198,g200)
    c: InternalAlignment(g198,g201)
    c: InternalAlignment(g199,g201)
    c: InternalAlignment(g200,g201)
    c: InternalAlignment(g202,g201)
    c: InternalAlignment(g203,g201)
    c: Weight(g204) = 1
    c: Equal(g204,g205)
    c: Equal(g204,g206)
    c: InternalAlignment(g204,g207)
    c: InternalAlignment(g205,g207)
    c: InternalAlignment(g206,g207)
    c: InternalAlignment(g208,g207)
    c: InternalAlignment(g209,g207)
    c: Block(g207)
    c: Block(g201)
    c: Coincident(g210,g201)
    c: Coincident(g210,g37)
    c: Coincident(g211,g37)
    c: Coincident(g211,g207)
    c: Coincident(g212,g207)
    c: Coincident(g212,g201)
    c: Vertical(g212)
    c: Horizontal(g213)
    c: Block(g213)
    c: Vertical(g214)
    c: Block(g214)
    c: Block(g215)
    c: Weight(g216) = 1
    c: Equal(g216,g217)
    c: Equal(g216,g218)
    c: InternalAlignment(g216,g219)
    c: InternalAlignment(g217,g219)
    c: InternalAlignment(g218,g219)
    c: InternalAlignment(g220,g219)
    c: InternalAlignment(g221,g219)
    c: Weight(g222) = 1
    c: Equal(g222,g223)
    c: Equal(g222,g224)
    c: InternalAlignment(g222,g225)
    c: InternalAlignment(g223,g225)
    c: InternalAlignment(g224,g225)
    c: InternalAlignment(g226,g225)
    c: InternalAlignment(g227,g225)
    c: Weight(g228) = 1
    c: Equal(g228,g229)
    c: Equal(g228,g230)
    c: InternalAlignment(g228,g231)
    c: InternalAlignment(g229,g231)
    c: InternalAlignment(g230,g231)
    c: InternalAlignment(g232,g231)
    c: InternalAlignment(g233,g231)
    c: Weight(g234) = 1
    c: Equal(g234,g235)
    c: Equal(g234,g236)
    c: InternalAlignment(g234,g237)
    c: InternalAlignment(g235,g237)
    c: InternalAlignment(g236,g237)
    c: InternalAlignment(g238,g237)
    c: InternalAlignment(g239,g237)
    c: Block(g219)
    c: Block(g225)
    c: Block(g231)
    c: Block(g237)
    c: Coincident(g240,g225)
    c: Coincident(g240,g219)
    c: Horizontal(g240)
    c: Block(g182)
    c: Weight(g241) = 1
    c: Equal(g241,g242)
    c: Equal(g241,g243)
    c: InternalAlignment(g241,g244)
    c: InternalAlignment(g242,g244)
    c: InternalAlignment(g243,g244)
    c: InternalAlignment(g245,g244)
    c: InternalAlignment(g246,g244)
    c: Weight(g247) = 1
    c: Equal(g247,g248)
    c: Equal(g247,g249)
    c: InternalAlignment(g247,g250)
    c: InternalAlignment(g248,g250)
    c: InternalAlignment(g249,g250)
    c: InternalAlignment(g251,g250)
    c: InternalAlignment(g252,g250)
    c: Block(g244)
    c: Block(g250)
    c: Coincident(g253,g244)
    c: Coincident(g253,g250)
    c: Weight(g254) = 1
    c: Equal(g254,g255)
    c: Equal(g254,g256)
    c: InternalAlignment(g254,g257)
    c: InternalAlignment(g255,g257)
    c: InternalAlignment(g256,g257)
    c: InternalAlignment(g258,g257)
    c: InternalAlignment(g259,g257)
    c: Weight(g260) = 1
    c: Equal(g260,g261)
    c: Equal(g260,g262)
    c: InternalAlignment(g260,g263)
    c: InternalAlignment(g261,g263)
    c: InternalAlignment(g262,g263)
    c: InternalAlignment(g264,g263)
    c: InternalAlignment(g265,g263)
    c: Weight(g266) = 1
    c: Equal(g266,g267)
    c: Equal(g266,g268)
    c: InternalAlignment(g266,g269)
    c: InternalAlignment(g267,g269)
    c: InternalAlignment(g268,g269)
    c: InternalAlignment(g270,g269)
    c: InternalAlignment(g271,g269)
    c: Block(g269)
    c: Block(g263)
    c: Block(g257)
    c: Coincident(g272,g263)
    c: Coincident(g272,g257)
    c: Coincident(g273,g257)
    c: Coincident(g273,g269)
    c: Vertical(g273)
    c: Coincident(g274,g269)
    c: Coincident(g274,g263)
    c: Horizontal(g274)
    c: Weight(g275) = 1
    c: Equal(g275,g276)
    c: InternalAlignment(g275,g277)
    c: InternalAlignment(g276,g277)
    c: InternalAlignment(g278,g277)
    c: InternalAlignment(g279,g277)
    c: Weight(g280) = 1
    c: InternalAlignment(g281,g283)
    c: InternalAlignment(g282,g283)
    c: InternalAlignment(g284,g283)
    c: InternalAlignment(g285,g283)
    c: Weight(g286) = 1
    c: Equal(g286,g287)
    c: Equal(g286,g288)
    c: InternalAlignment(g286,g289)
    c: InternalAlignment(g287,g289)
    c: InternalAlignment(g288,g289)
    c: InternalAlignment(g290,g289)
    c: InternalAlignment(g291,g289)
    c: Equal(g292,g293)
    c: Equal(g292,g294)
    c: InternalAlignment(g292,g295)
    c: InternalAlignment(g293,g295)
    c: InternalAlignment(g294,g295)
    c: InternalAlignment(g296,g295)
    c: InternalAlignment(g297,g295)
    c: Block(g283)
    c: Block(g289)
    c: Block(g295)
    c: Block(g277)
    c: Coincident(g298,g277)
    c: Coincident(g298,g283)
    c: Horizontal(g298)
    c: Coincident(g299,g283)
    c: Coincident(g299,g289)
    c: Vertical(g299)
    c: Coincident(g300,g289)
    c: Coincident(g300,g295)
    c: Horizontal(g300)
    c: Coincident(g301,g295)
    c: Coincident(g301,g277)
    c: Weight(g302) = 1
    c: Equal(g302,g303)
    c: Equal(g302,g304)
    c: InternalAlignment(g302,g305)
    c: InternalAlignment(g303,g305)
    c: InternalAlignment(g304,g305)
    c: InternalAlignment(g306,g305)
    c: InternalAlignment(g307,g305)
    c: Weight(g308) = 1
    c: Equal(g308,g309)
    c: Equal(g308,g310)
    c: InternalAlignment(g308,g311)
    c: InternalAlignment(g309,g311)
    c: InternalAlignment(g310,g311)
    c: InternalAlignment(g312,g311)
    c: Weight(g314) = 1
    c: Equal(g314,g315)
    c: Equal(g314,g316)
    c: InternalAlignment(g314,g317)
    c: InternalAlignment(g315,g317)
    c: InternalAlignment(g316,g317)
    c: InternalAlignment(g318,g317)
    c: InternalAlignment(g319,g317)
    c: Block(g317)
    c: Block(g311)
    c: Block(g305)
    c: Coincident(g320,g317)
    c: Coincident(g320,g311)
    c: Horizontal(g320)
    c: Coincident(g321,g311)
    c: Coincident(g321,g305)
    c: Vertical(g321)
    c: Coincident(g322,g305)
    c: Coincident(g322,g317)
    c: InternalAlignment(g323,g324)
    c: InternalAlignment(g325,g324)
    c: InternalAlignment(g326,g324)
    c: Block(g324)
    c: Equal(g327,g328)
    c: Equal(g327,g329)
    c: InternalAlignment(g327,g330)
    c: InternalAlignment(g328,g330)
    c: InternalAlignment(g329,g330)
    c: InternalAlignment(g331,g330)
    c: InternalAlignment(g332,g330)
    c: Block(g330)
    c: Coincident(g333,g324)
    c: Horizontal(g333)
    c: Block(g333)
    c: Coincident(g334,g324)
    c: Coincident(g334,g250)
    c: Vertical(g334)
    c: Coincident(g335,g330)
    c: Coincident(g335,g244)
    c: Vertical(g335)
    c: Block(g336)
    c: Block(g2)
    c: Distance(g334) = 119.89
    c: Coincident(g337,g336)
    c: Coincident(g337,g2)
    c: Coincident(g338,g2)
    c: Coincident(g338,g336)
    c: Block(g3)
    c: Block(g339)
    c: Coincident(g340,g339)
    c: Coincident(g340,g3)
    c: Coincident(g341,g339)
    c: Coincident(g341,g3)
    c: Block(g341)
    c: Block(g340)
    c: Weight(g342) = 1
    c: Equal(g342,g343)
    c: Equal(g342,g344)
    c: InternalAlignment(g342,g345)
    c: InternalAlignment(g343,g345)
    c: InternalAlignment(g344,g345)
    c: InternalAlignment(g346,g345)
    c: InternalAlignment(g347,g345)
    c: Weight(g348) = 1
    c: Equal(g348,g349)
    c: Equal(g348,g350)
    c: InternalAlignment(g348,g351)
    c: InternalAlignment(g349,g351)
    c: InternalAlignment(g350,g351)
    c: InternalAlignment(g352,g351)
    c: InternalAlignment(g353,g351)
    c: Weight(g354) = 1
    c: Equal(g354,g355)
    c: Equal(g354,g356)
    c: InternalAlignment(g354,g357)
    c: InternalAlignment(g355,g357)
    c: InternalAlignment(g356,g357)
    c: InternalAlignment(g358,g357)
    c: InternalAlignment(g359,g357)
    c: Weight(g360) = 1
    c: Equal(g360,g361)
    c: Equal(g360,g362)
    c: InternalAlignment(g360,g363)
    c: InternalAlignment(g361,g363)
    c: InternalAlignment(g362,g363)
    c: InternalAlignment(g364,g363)
    c: InternalAlignment(g365,g363)
    c: Block(g363)
    c: Block(g357)
    c: Block(g351)
    c: Block(g345)
    c: Coincident(g366,g363)
    c: Coincident(g366,g345)
    c: Vertical(g366)
    c: Coincident(g367,g345)
    c: Coincident(g367,g351)
    c: Coincident(g368,g351)
    c: Coincident(g368,g357)
    c: Vertical(g368)
    c: Coincident(g369,g357)
    c: Coincident(g369,g363)
    c: Horizontal(g369)
    c: Vertical(g370)
    c: Vertical(g371)
    c: Vertical(g372)
    c: Vertical(g373)
    c: Coincident(g374,g0)
    c: Coincident(g374,g1)
    c: Horizontal(g374)
    c: Block(g374)
    c: Distance(g374) = 450
    c: Block(g372)
    c: Block(g370)
    c: Block(g371)
    c: Block(g373)
    c: Distance(g0) = 240
    c: Horizontal(g375)
    c: Distance(g375) = 12
    c: Coincident(g375,g370)
    c: Vertical(g376)
    c: Distance(g376) = 12
    c: Coincident(g376,g370)
    c: Coincident(g377,g375)
    c: Vertical(g377)
    c: Horizontal(g378)
    c: Vertical(g379)
    c: Distance(g379) = 6
    c: Coincident(g379,g375)
    c: Coincident(g378,g375)
    c: Block(g377)
    c: Coincident(g380,g377)
    c: Horizontal(g380)
    c: Distance(g380) = 6
    c: Vertical(g381)
    c: Distance(g381) = 3
    c: Vertical(g382)
    c: Distance(g382) = 3
    c: Coincident(g382,g370)
    c: Coincident(g376,g381)
    c: Coincident(g388,g382)
    c: Weight(g383) = 1
    c: Equal(g383,g384)
    c: Coincident(g384,g378)
    c: Equal(g383,g385)
    c: Coincident(g385,g379)
    c: Equal(g383,g386)
    c: Coincident(g386,g380)
    c: Equal(g383,g387)
    c: Coincident(g388,g381)
    c: InternalAlignment(g383-g387 -> g388) x5
    c: InternalAlignment(g389,g388)
    c: InternalAlignment(g390,g388)
    c: InternalAlignment(g391,g388)
    c: Coincident(g392,g164)
    c: Coincident(g392,g158)
    c: Horizontal(g392)
    c: Block(g388)
    c: Vertical(g393)
    c: Distance(g393) = 12
    c: Coincident(g393,g371)
    c: Horizontal(g394)
    c: Distance(g394) = 12
    c: Coincident(g394,g371)
    c: Coincident(g395,g394)
    c: Vertical(g395)
    c: Distance(g395) = 12
    c: Coincident(g396,g395)
    c: Horizontal(g396)
    c: Distance(g396) = 6
    c: Horizontal(g397)
    c: Distance(g397) = 6
FEATURE [Part::Extrusion] Extrude005
  Base = -> Sketch003
  Dir = (0,0,1)
  DirMode = 2
  FaceMakerClass = Part::FaceMakerBullseye
  LengthFwd = 24
  LengthRev = 0
  Solid = true
  Symmetric = false
